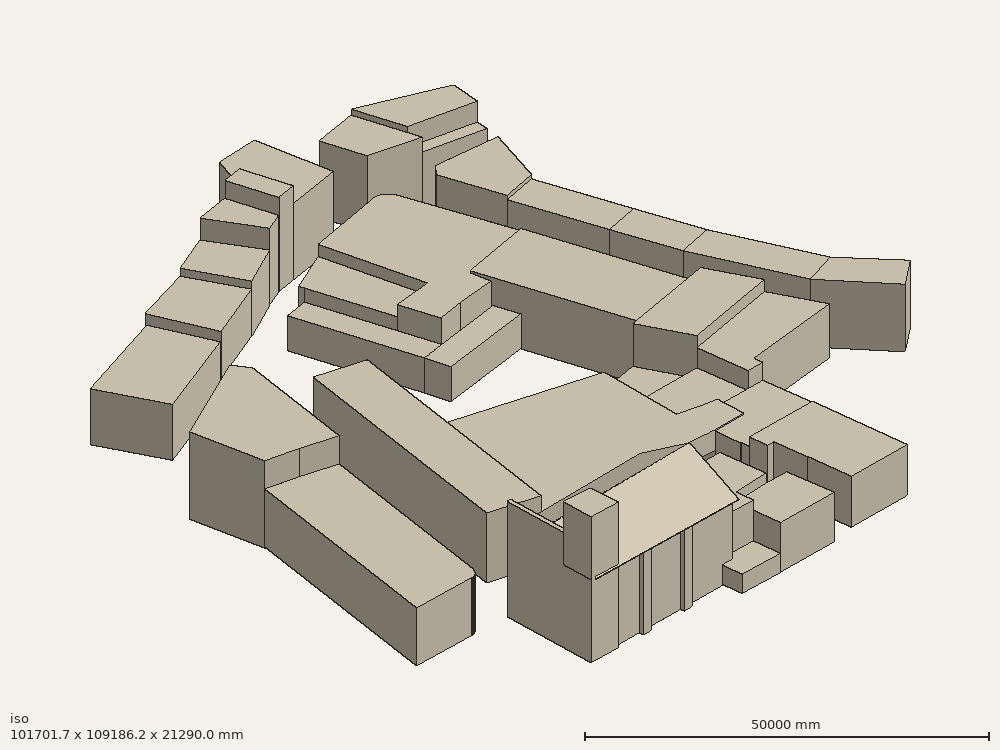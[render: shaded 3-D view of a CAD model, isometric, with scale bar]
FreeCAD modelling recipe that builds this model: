
FCSTD DOCUMENT  (FreeCAD 0.16R6563 (Git))
Label: Levantamento
License: All rights reserved
LicenseURL: http://en.wikipedia.org/wiki/All_rights_reserved
objects: App::Annotation×611, Part::Feature×158, Part::Part2DObjectPython×64, Part::Extrusion×37, App::DocumentObjectGroup×7, Part::FeaturePython×7, App::FeaturePython×4, Part::Cut×2, Part::Compound×1, Part::MultiFuse×1, App::DocumentObjectGroupPython×1
note: 273 computed .brp shape members not serialized (recipe doc carries the construction recipe); baked Part::Feature solids carry a one-line shape summary decoded from their .brp

FEATURE [App::Annotation] Text
  LabelText = TRAVESSA DE S.TIAGO
  Position = (-9.7511e+07,-6.33971e+07,25950)
FEATURE [App::Annotation] Text001
  LabelText = LARGO DR. JUSTINO FREIRE
  Position = (-9.75583e+07,-6.3388e+07,26154)
FEATURE [App::Annotation] Text002
  LabelText = RUA DO ALEIXO
  Position = (-9.75352e+07,-6.33613e+07,25958)
FEATURE [App::Annotation] Text003
  LabelText = RUA DO TERREIRINHO
  Position = (-9.75126e+07,-6.33096e+07,25667)
FEATURE [App::Annotation] Text004
  LabelText = RUA SERPA PINTO
  Position = (-9.74773e+07,-6.3325e+07,26806)
FEATURE [App::Annotation] Text005
  LabelText = IGREJA DE S. TIAGO
  Position = (-9.75165e+07,-6.33832e+07,25950)
FEATURE [App::Annotation] Text006
  LabelText = -97400
  Position = (-9.74009e+07,-6.34097e+07,0)
FEATURE [App::Annotation] Text007
  LabelText = -97450
  Position = (-9.74508e+07,-6.34097e+07,0)
FEATURE [App::Annotation] Text008
  LabelText = -97500
  Position = (-9.75009e+07,-6.34097e+07,0)
FEATURE [App::Annotation] Text009
  LabelText = -97550
  Position = (-9.75507e+07,-6.34097e+07,0)
FEATURE [App::Annotation] Text010
  LabelText = -63400
  Position = (-9.73992e+07,-6.33989e+07,0)
FEATURE [App::Annotation] Text011
  LabelText = -63350
  Position = (-9.73992e+07,-6.33486e+07,0)
FEATURE [App::Annotation] Text012
  LabelText = -63300
  Position = (-9.73992e+07,-6.32985e+07,0)
FEATURE [App::Annotation] Text013
  LabelText = VD
  Position = (-9.75235e+07,-6.33229e+07,0)
FEATURE [App::Annotation] Text014
  LabelText = 25.74
  Position = (-9.75242e+07,-6.33231e+07,0)
FEATURE [App::Annotation] Text015
  LabelText = IN
  Position = (-9.75237e+07,-6.33233e+07,0)
FEATURE [App::Annotation] Text016
  LabelText = 25.75
  Position = (-9.75244e+07,-6.33234e+07,0)
FEATURE [App::Annotation] Text017
  LabelText = LNMRVD
  Position = (-9.75268e+07,-6.3332e+07,0)
FEATURE [App::Annotation] Text018
  LabelText = 25.79
  Position = (-9.75274e+07,-6.33329e+07,0)
FEATURE [App::Annotation] Text019
  LabelText = LN
  Position = (-9.7528e+07,-6.33353e+07,0)
FEATURE [App::Annotation] Text020
  LabelText = 25.72
  Position = (-9.75287e+07,-6.33356e+07,0)
FEATURE [App::Annotation] Text021
  LabelText = 26.02
  Position = (-9.7542e+07,-6.33754e+07,0)
FEATURE [App::Annotation] Text022
  LabelText = CX
  Position = (-9.75309e+07,-6.33164e+07,0)
FEATURE [App::Annotation] Text023
  LabelText = 25.70
  Position = (-9.75313e+07,-6.33168e+07,0)
FEATURE [App::Annotation] Text024
  LabelText = CX
  Position = (-9.75307e+07,-6.33169e+07,0)
FEATURE [App::Annotation] Text025
  LabelText = 25.63
  Position = (-9.75311e+07,-6.33173e+07,0)
FEATURE [App::Annotation] Text026
  LabelText = CX
  Position = (-9.75311e+07,-6.3317e+07,0)
FEATURE [App::Annotation] Text027
  LabelText = 25.63
  Position = (-9.75315e+07,-6.33174e+07,0)
FEATURE [App::Annotation] Text028
  LabelText = CC
  Position = (-9.7534e+07,-6.33179e+07,0)
FEATURE [App::Annotation] Text029
  LabelText = 25.76
  Position = (-9.75346e+07,-6.33182e+07,0)
FEATURE [App::Annotation] Text030
  LabelText = OL
  Position = (-9.75349e+07,-6.33183e+07,0)
FEATURE [App::Annotation] Text031
  LabelText = 26.00
  Position = (-9.75356e+07,-6.33185e+07,0)
FEATURE [App::Annotation] Text032
  LabelText = OL
  Position = (-9.75364e+07,-6.3319e+07,0)
FEATURE [App::Annotation] Text033
  LabelText = 26.00
  Position = (-9.75371e+07,-6.33193e+07,0)
FEATURE [App::Annotation] Text034
  LabelText = LNCC
  Position = (-9.7539e+07,-6.33199e+07,0)
FEATURE [App::Annotation] Text035
  LabelText = 25.84
  Position = (-9.75396e+07,-6.33204e+07,0)
FEATURE [App::Annotation] Text036
  LabelText = LN
  Position = (-9.75385e+07,-6.33211e+07,0)
FEATURE [App::Annotation] Text037
  LabelText = 25.73
  Position = (-9.75392e+07,-6.33213e+07,0)
FEATURE [App::Annotation] Text038
  LabelText = CTT
  Position = (-9.75428e+07,-6.33239e+07,0)
FEATURE [App::Annotation] Text039
  LabelText = 25.88
  Position = (-9.75435e+07,-6.33242e+07,0)
FEATURE [App::Annotation] Text040
  LabelText = CTT
  Position = (-9.75436e+07,-6.33243e+07,0)
FEATURE [App::Annotation] Text041
  LabelText = 25.88
  Position = (-9.75442e+07,-6.33246e+07,0)
FEATURE [App::Annotation] Text042
  LabelText = CTT
  Position = (-9.75439e+07,-6.33237e+07,0)
FEATURE [App::Annotation] Text043
  LabelText = 25.87
  Position = (-9.75445e+07,-6.3324e+07,0)
FEATURE [App::Annotation] Text044
  LabelText = SOL
  Position = (-9.75449e+07,-6.33228e+07,0)
FEATURE [App::Annotation] Text045
  LabelText = 26.13
  Position = (-9.75455e+07,-6.33231e+07,0)
FEATURE [App::Annotation] Text046
  LabelText = LN
  Position = (-9.75498e+07,-6.33263e+07,0)
FEATURE [App::Annotation] Text047
  LabelText = 25.92
  Position = (-9.75505e+07,-6.33265e+07,0)
FEATURE [App::Annotation] Text048
  LabelText = CC
  Position = (-9.75503e+07,-6.33253e+07,0)
FEATURE [App::Annotation] Text049
  LabelText = 26.11
  Position = (-9.75509e+07,-6.33256e+07,0)
FEATURE [App::Annotation] Text050
  LabelText = OL
  Position = (-9.75518e+07,-6.3326e+07,0)
FEATURE [App::Annotation] Text051
  LabelText = 26.19
  Position = (-9.75524e+07,-6.33263e+07,0)
FEATURE [App::Annotation] Text052
  LabelText = CC
  Position = (-9.75559e+07,-6.33278e+07,0)
FEATURE [App::Annotation] Text053
  LabelText = 26.12
  Position = (-9.75565e+07,-6.3328e+07,0)
FEATURE [App::Annotation] Text054
  LabelText = LN
  Position = (-9.75554e+07,-6.33287e+07,0)
FEATURE [App::Annotation] Text055
  LabelText = 25.90
  Position = (-9.75561e+07,-6.33289e+07,0)
FEATURE [App::Annotation] Text056
  LabelText = INH
  Position = (-9.75539e+07,-6.3334e+07,0)
FEATURE [App::Annotation] Text057
  LabelText = 25.92
  Position = (-9.75546e+07,-6.33343e+07,0)
FEATURE [App::Annotation] Text058
  LabelText = INH
  Position = (-9.75549e+07,-6.33321e+07,0)
FEATURE [App::Annotation] Text059
  LabelText = 26.04
  Position = (-9.75555e+07,-6.33324e+07,0)
FEATURE [App::Annotation] Text060
  LabelText = INH
  Position = (-9.75501e+07,-6.33302e+07,0)
FEATURE [App::Annotation] Text061
  LabelText = 26.05
  Position = (-9.75508e+07,-6.33305e+07,0)
FEATURE [App::Annotation] Text062
  LabelText = INH
  Position = (-9.75369e+07,-6.33231e+07,0)
FEATURE [App::Annotation] Text063
  LabelText = 25.84
  Position = (-9.75376e+07,-6.33234e+07,0)
FEATURE [App::Annotation] Text064
  LabelText = INH
  Position = (-9.75357e+07,-6.33232e+07,0)
FEATURE [App::Annotation] Text065
  LabelText = 25.82
  Position = (-9.75363e+07,-6.33235e+07,0)
FEATURE [App::Annotation] Text066
  LabelText = INH
  Position = (-9.75336e+07,-6.33221e+07,0)
FEATURE [App::Annotation] Text067
  LabelText = 25.76
  Position = (-9.75343e+07,-6.33224e+07,0)
FEATURE [App::Annotation] Text068
  LabelText = OL
  Position = (-9.7533e+07,-6.33256e+07,0)
FEATURE [App::Annotation] Text069
  LabelText = 26.42
  Position = (-9.75337e+07,-6.33259e+07,0)
FEATURE [App::Annotation] Text070
  LabelText = IN
  Position = (-9.75314e+07,-6.33278e+07,0)
FEATURE [App::Annotation] Text071
  LabelText = 25.89
  Position = (-9.7532e+07,-6.33279e+07,0)
FEATURE [App::Annotation] Text072
  LabelText = CC
  Position = (-9.75315e+07,-6.33268e+07,0)
FEATURE [App::Annotation] Text073
  LabelText = 25.89
  Position = (-9.75322e+07,-6.33271e+07,0)
FEATURE [App::Annotation] Text074
  LabelText = CC
  Position = (-9.75329e+07,-6.33242e+07,0)
FEATURE [App::Annotation] Text075
  LabelText = 25.84
  Position = (-9.75336e+07,-6.33245e+07,0)
FEATURE [App::Annotation] Text076
  LabelText = CC
  Position = (-9.75382e+07,-6.33271e+07,0)
FEATURE [App::Annotation] Text077
  LabelText = 25.93
  Position = (-9.75388e+07,-6.33273e+07,0)
FEATURE [App::Annotation] Text078
  LabelText = UM
  Position = (-9.75385e+07,-6.33265e+07,0)
FEATURE [App::Annotation] Text079
  LabelText = 25.76
  Position = (-9.75392e+07,-6.33268e+07,0)
FEATURE [App::Annotation] Text080
  LabelText = UM
  Position = (-9.75319e+07,-6.33228e+07,0)
FEATURE [App::Annotation] Text081
  LabelText = 25.67
  Position = (-9.75326e+07,-6.33231e+07,0)
FEATURE [App::Annotation] Text082
  LabelText = UM
  Position = (-9.75313e+07,-6.33232e+07,0)
FEATURE [App::Annotation] Text083
  LabelText = 25.67
  Position = (-9.7532e+07,-6.33235e+07,0)
FEATURE [App::Annotation] Text084
  LabelText = LN
  Position = (-9.75323e+07,-6.33233e+07,0)
FEATURE [App::Annotation] Text085
  LabelText = 25.68
  Position = (-9.7533e+07,-6.33235e+07,0)
FEATURE [App::Annotation] Text086
  LabelText = LN
  Position = (-9.75315e+07,-6.33235e+07,0)
FEATURE [App::Annotation] Text087
  LabelText = 25.72
  Position = (-9.75322e+07,-6.33238e+07,0)
FEATURE [App::Annotation] Text088
  LabelText = LN
  Position = (-9.75305e+07,-6.33251e+07,0)
FEATURE [App::Annotation] Text089
  LabelText = 25.75
  Position = (-9.75311e+07,-6.33253e+07,0)
FEATURE [App::Annotation] Text090
  LabelText = LN
  Position = (-9.75301e+07,-6.33276e+07,0)
FEATURE [App::Annotation] Text091
  LabelText = 25.72
  Position = (-9.75307e+07,-6.33279e+07,0)
FEATURE [App::Annotation] Text092
  LabelText = VD
  Position = (-9.75244e+07,-6.33212e+07,0)
FEATURE [App::Annotation] Text093
  LabelText = 25.72
  Position = (-9.75251e+07,-6.33214e+07,0)
FEATURE [App::Annotation] Text094
  LabelText = CXD
  Position = (-9.75204e+07,-6.33159e+07,0)
FEATURE [App::Annotation] Text095
  LabelText = 25.67
  Position = (-9.75207e+07,-6.33163e+07,0)
FEATURE [App::Annotation] Text096
  LabelText = VD
  Position = (-9.75183e+07,-6.33166e+07,0)
FEATURE [App::Annotation] Text097
  LabelText = 25.58
  Position = (-9.7519e+07,-6.33169e+07,0)
FEATURE [App::Annotation] Text098
  LabelText = OL
  Position = (-9.75059e+07,-6.33029e+07,0)
FEATURE [App::Annotation] Text099
  LabelText = 25.84
  Position = (-9.75065e+07,-6.33031e+07,0)
FEATURE [App::Annotation] Text100
  LabelText = OL
  Position = (-9.75043e+07,-6.33022e+07,0)
FEATURE [App::Annotation] Text101
  LabelText = 25.94
  Position = (-9.75049e+07,-6.33025e+07,0)
FEATURE [App::Annotation] Text102
  LabelText = CXE
  Position = (-9.7504e+07,-6.33017e+07,0)
FEATURE [App::Annotation] Text103
  LabelText = 25.84
  Position = (-9.75043e+07,-6.33021e+07,0)
FEATURE [App::Annotation] Text104
  LabelText = CXE
  Position = (-9.75038e+07,-6.3302e+07,0)
FEATURE [App::Annotation] Text105
  LabelText = 25.79
  Position = (-9.75041e+07,-6.33024e+07,0)
FEATURE [App::Annotation] Text106
  LabelText = CXE
  Position = (-9.7503e+07,-6.33016e+07,0)
FEATURE [App::Annotation] Text107
  LabelText = 25.80
  Position = (-9.75033e+07,-6.3302e+07,0)
FEATURE [App::Annotation] Text108
  LabelText = OL
  Position = (-9.7499e+07,-6.32997e+07,0)
FEATURE [App::Annotation] Text109
  LabelText = 26.17
  Position = (-9.74996e+07,-6.32999e+07,0)
FEATURE [App::Annotation] Text110
  LabelText = CXD
  Position = (-9.75007e+07,-6.33004e+07,0)
FEATURE [App::Annotation] Text111
  LabelText = 25.85
  Position = (-9.7501e+07,-6.3301e+07,0)
FEATURE [App::Annotation] Text112
  LabelText = CXD
  Position = (-9.74978e+07,-6.32998e+07,0)
FEATURE [App::Annotation] Text113
  LabelText = 25.86
  Position = (-9.74982e+07,-6.33003e+07,0)
FEATURE [App::Annotation] Text114
  LabelText = UM
  Position = (-9.74967e+07,-6.33e+07,0)
FEATURE [App::Annotation] Text115
  LabelText = 25.80
  Position = (-9.74974e+07,-6.33003e+07,0)
FEATURE [App::Annotation] Text116
  LabelText = UM
  Position = (-9.74961e+07,-6.32999e+07,0)
FEATURE [App::Annotation] Text117
  LabelText = 25.79
  Position = (-9.74968e+07,-6.33001e+07,0)
FEATURE [App::Annotation] Text118
  LabelText = IN
  Position = (-9.74906e+07,-6.32984e+07,0)
FEATURE [App::Annotation] Text119
  LabelText = 26.00
  Position = (-9.74913e+07,-6.32985e+07,0)
FEATURE [App::Annotation] Text120
  LabelText = CC
  Position = (-9.74881e+07,-6.32975e+07,0)
FEATURE [App::Annotation] Text121
  LabelText = 26.01
  Position = (-9.74887e+07,-6.32978e+07,0)
FEATURE [App::Annotation] Text122
  LabelText = VD
  Position = (-9.74883e+07,-6.33016e+07,0)
FEATURE [App::Annotation] Text123
  LabelText = 26.02
  Position = (-9.7489e+07,-6.33019e+07,0)
FEATURE [App::Annotation] Text124
  LabelText = VD
  Position = (-9.74956e+07,-6.33036e+07,0)
FEATURE [App::Annotation] Text125
  LabelText = 25.93
  Position = (-9.74963e+07,-6.33039e+07,0)
FEATURE [App::Annotation] Text126
  LabelText = VD
  Position = (-9.74956e+07,-6.33036e+07,0)
FEATURE [App::Annotation] Text127
  LabelText = 25.93
  Position = (-9.74963e+07,-6.33039e+07,0)
FEATURE [App::Annotation] Text128
  LabelText = CXD
  Position = (-9.75007e+07,-6.33052e+07,0)
FEATURE [App::Annotation] Text129
  LabelText = 25.82
  Position = (-9.7501e+07,-6.33056e+07,0)
FEATURE [App::Annotation] Text130
  LabelText = VD
  Position = (-9.75015e+07,-6.33054e+07,0)
FEATURE [App::Annotation] Text131
  LabelText = 25.83
  Position = (-9.75022e+07,-6.33057e+07,0)
FEATURE [App::Annotation] Text132
  LabelText = VD
  Position = (-9.75047e+07,-6.33071e+07,0)
FEATURE [App::Annotation] Text133
  LabelText = 25.76
  Position = (-9.75053e+07,-6.33073e+07,0)
FEATURE [App::Annotation] Text134
  LabelText = CC
  Position = (-9.74996e+07,-6.33064e+07,0)
FEATURE [App::Annotation] Text135
  LabelText = 25.89
  Position = (-9.75003e+07,-6.33067e+07,0)
FEATURE [App::Annotation] Text136
  LabelText = VD
  Position = (-9.75005e+07,-6.33068e+07,0)
FEATURE [App::Annotation] Text137
  LabelText = 25.84
  Position = (-9.75012e+07,-6.3307e+07,0)
FEATURE [App::Annotation] Text138
  LabelText = MRVD
  Position = (-9.75264e+07,-6.33325e+07,0)
FEATURE [App::Annotation] Text139
  LabelText = 26.39
  Position = (-9.7527e+07,-6.33331e+07,0)
FEATURE [App::Annotation] Text140
  LabelText = CT
  Position = (-9.75249e+07,-6.33283e+07,0)
FEATURE [App::Annotation] Text141
  LabelText = 26.35
  Position = (-9.75255e+07,-6.33286e+07,0)
FEATURE [App::Annotation] Text142
  LabelText = CT
  Position = (-9.75222e+07,-6.33238e+07,0)
FEATURE [App::Annotation] Text143
  LabelText = 26.29
  Position = (-9.75229e+07,-6.3324e+07,0)
FEATURE [App::Annotation] Text144
  LabelText = CT
  Position = (-9.75189e+07,-6.33204e+07,0)
FEATURE [App::Annotation] Text145
  LabelText = 26.22
  Position = (-9.75196e+07,-6.33206e+07,0)
FEATURE [App::Annotation] Text146
  LabelText = CT
  Position = (-9.75162e+07,-6.33183e+07,0)
FEATURE [App::Annotation] Text147
  LabelText = 26.20
  Position = (-9.75169e+07,-6.33186e+07,0)
FEATURE [App::Annotation] Text148
  LabelText = CT
  Position = (-9.75164e+07,-6.33162e+07,0)
FEATURE [App::Annotation] Text149
  LabelText = 26.04
  Position = (-9.75171e+07,-6.33165e+07,0)
FEATURE [App::Annotation] Text150
  LabelText = CT
  Position = (-9.75151e+07,-6.33153e+07,0)
FEATURE [App::Annotation] Text151
  LabelText = 26.08
  Position = (-9.75157e+07,-6.33155e+07,0)
FEATURE [App::Annotation] Text152
  LabelText = IL
  Position = (-9.75163e+07,-6.33171e+07,0)
FEATURE [App::Annotation] Text153
  LabelText = 26.13
  Position = (-9.75169e+07,-6.33173e+07,0)
FEATURE [App::Annotation] Text154
  LabelText = IL
  Position = (-9.75157e+07,-6.3316e+07,0)
FEATURE [App::Annotation] Text155
  LabelText = 26.09
  Position = (-9.75164e+07,-6.33161e+07,0)
FEATURE [App::Annotation] Text156
  LabelText = CC
  Position = (-9.75107e+07,-6.33057e+07,0)
FEATURE [App::Annotation] Text157
  LabelText = 25.68
  Position = (-9.75113e+07,-6.3306e+07,0)
FEATURE [App::Annotation] Text158
  LabelText = AT
  Position = (-9.75124e+07,-6.33068e+07,0)
FEATURE [App::Annotation] Text159
  LabelText = 25.58
  Position = (-9.75131e+07,-6.33071e+07,0)
FEATURE [App::Annotation] Text160
  LabelText = OL
  Position = (-9.75161e+07,-6.33083e+07,0)
FEATURE [App::Annotation] Text161
  LabelText = 25.81
  Position = (-9.75167e+07,-6.33085e+07,0)
FEATURE [App::Annotation] Text162
  LabelText = AT
  Position = (-9.75195e+07,-6.33102e+07,0)
FEATURE [App::Annotation] Text163
  LabelText = 25.48
  Position = (-9.75202e+07,-6.33104e+07,0)
FEATURE [App::Annotation] Text164
  LabelText = CXCTT
  Position = (-9.75202e+07,-6.331e+07,0)
FEATURE [App::Annotation] Text165
  LabelText = 25.48
  Position = (-9.75202e+07,-6.33104e+07,0)
FEATURE [App::Annotation] Text166
  LabelText = CXCTT
  Position = (-9.75206e+07,-6.33102e+07,0)
FEATURE [App::Annotation] Text167
  LabelText = 25.47
  Position = (-9.75206e+07,-6.33106e+07,0)
FEATURE [App::Annotation] Text168
  LabelText = UM
  Position = (-9.75203e+07,-6.33103e+07,0)
FEATURE [App::Annotation] Text169
  LabelText = 25.38
  Position = (-9.7521e+07,-6.33106e+07,0)
FEATURE [App::Annotation] Text170
  LabelText = CC
  Position = (-9.75208e+07,-6.33104e+07,0)
FEATURE [App::Annotation] Text171
  LabelText = 25.47
  Position = (-9.75214e+07,-6.33106e+07,0)
FEATURE [App::Annotation] Text172
  LabelText = CTT
  Position = (-9.7521e+07,-6.33111e+07,0)
FEATURE [App::Annotation] Text173
  LabelText = 25.54
  Position = (-9.75216e+07,-6.33115e+07,0)
FEATURE [App::Annotation] Text174
  LabelText = CTT
  Position = (-9.75215e+07,-6.33114e+07,0)
FEATURE [App::Annotation] Text175
  LabelText = 25.57
  Position = (-9.75222e+07,-6.33118e+07,0)
FEATURE [App::Annotation] Text176
  LabelText = CTT
  Position = (-9.7522e+07,-6.33107e+07,0)
FEATURE [App::Annotation] Text177
  LabelText = 25.55
  Position = (-9.75226e+07,-6.3311e+07,0)
FEATURE [App::Annotation] Text178
  LabelText = CC
  Position = (-9.75249e+07,-6.33104e+07,0)
FEATURE [App::Annotation] Text179
  LabelText = 25.65
  Position = (-9.75256e+07,-6.33106e+07,0)
FEATURE [App::Annotation] Text180
  LabelText = OL
  Position = (-9.75244e+07,-6.33121e+07,0)
FEATURE [App::Annotation] Text181
  LabelText = 26.10
  Position = (-9.7525e+07,-6.33123e+07,0)
FEATURE [App::Annotation] Text182
  LabelText = G
  Position = (-9.7524e+07,-6.33116e+07,0)
FEATURE [App::Annotation] Text183
  LabelText = 25.61
  Position = (-9.75246e+07,-6.33117e+07,0)
FEATURE [App::Annotation] Text184
  LabelText = G
  Position = (-9.75238e+07,-6.33122e+07,0)
FEATURE [App::Annotation] Text185
  LabelText = G
  Position = (-9.7524e+07,-6.33123e+07,0)
FEATURE [App::Annotation] Text186
  LabelText = CC
  Position = (-9.75238e+07,-6.33134e+07,0)
FEATURE [App::Annotation] Text187
  LabelText = 25.54
  Position = (-9.75245e+07,-6.33136e+07,0)
FEATURE [App::Annotation] Text188
  LabelText = UM
  Position = (-9.75246e+07,-6.33138e+07,0)
FEATURE [App::Annotation] Text189
  LabelText = 25.52
  Position = (-9.75253e+07,-6.33141e+07,0)
FEATURE [App::Annotation] Text190
  LabelText = SOL
  Position = (-9.75262e+07,-6.33143e+07,0)
FEATURE [App::Annotation] Text191
  LabelText = 25.98
  Position = (-9.75268e+07,-6.33146e+07,0)
FEATURE [App::Annotation] Text192
  LabelText = CXE
  Position = (-9.75276e+07,-6.33148e+07,0)
FEATURE [App::Annotation] Text193
  LabelText = 25.69
  Position = (-9.75279e+07,-6.33152e+07,0)
FEATURE [App::Annotation] Text194
  LabelText = CXE
  Position = (-9.75275e+07,-6.33151e+07,0)
FEATURE [App::Annotation] Text195
  LabelText = 25.63
  Position = (-9.75278e+07,-6.33155e+07,0)
FEATURE [App::Annotation] Text196
  LabelText = CXE
  Position = (-9.75282e+07,-6.33154e+07,0)
FEATURE [App::Annotation] Text197
  LabelText = 25.63
  Position = (-9.75286e+07,-6.33158e+07,0)
FEATURE [App::Annotation] Text198
  LabelText = VD
  Position = (-9.75189e+07,-6.33146e+07,0)
FEATURE [App::Annotation] Text199
  LabelText = 25.64
  Position = (-9.75196e+07,-6.33149e+07,0)
FEATURE [App::Annotation] Text200
  LabelText = VD
  Position = (-9.75178e+07,-6.33139e+07,0)
FEATURE [App::Annotation] Text201
  LabelText = 25.69
  Position = (-9.75185e+07,-6.33141e+07,0)
FEATURE [App::Annotation] Text202
  LabelText = VD
  Position = (-9.75147e+07,-6.33122e+07,0)
FEATURE [App::Annotation] Text203
  LabelText = 25.65
  Position = (-9.75154e+07,-6.33124e+07,0)
FEATURE [App::Annotation] Text204
  LabelText = 25.59
  Position = (-9.75159e+07,-6.3314e+07,0)
FEATURE [App::Annotation] Text205
  LabelText = VD
  Position = (-9.75151e+07,-6.33139e+07,0)
FEATURE [App::Annotation] Text206
  LabelText = 25.60
  Position = (-9.75158e+07,-6.33142e+07,0)
FEATURE [App::Annotation] Text207
  LabelText = G
  Position = (-9.75151e+07,-6.33144e+07,0)
FEATURE [App::Annotation] Text208
  LabelText = 25.62
  Position = (-9.75158e+07,-6.33145e+07,0)
FEATURE [App::Annotation] Text209
  LabelText = G
  Position = (-9.7515e+07,-6.33146e+07,0)
FEATURE [App::Annotation] Text210
  LabelText = 25.81
  Position = (-9.75156e+07,-6.33147e+07,0)
FEATURE [App::Annotation] Text211
  LabelText = G
  Position = (-9.75148e+07,-6.3315e+07,0)
FEATURE [App::Annotation] Text212
  LabelText = 26.13
  Position = (-9.75154e+07,-6.33151e+07,0)
FEATURE [App::Annotation] Text213
  LabelText = G
  Position = (-9.75121e+07,-6.33136e+07,0)
FEATURE [App::Annotation] Text214
  LabelText = 26.12
  Position = (-9.75128e+07,-6.33137e+07,0)
FEATURE [App::Annotation] Text215
  LabelText = G
  Position = (-9.75123e+07,-6.33134e+07,0)
FEATURE [App::Annotation] Text216
  LabelText = 25.82
  Position = (-9.7513e+07,-6.33135e+07,0)
FEATURE [App::Annotation] Text217
  LabelText = G
  Position = (-9.75124e+07,-6.33131e+07,0)
FEATURE [App::Annotation] Text218
  LabelText = 25.65
  Position = (-9.75131e+07,-6.33132e+07,0)
FEATURE [App::Annotation] Text219
  LabelText = AMP
  Position = (-9.75137e+07,-6.33114e+07,0)
FEATURE [App::Annotation] Text220
  LabelText = 25.69
  Position = (-9.75144e+07,-6.33119e+07,0)
FEATURE [App::Annotation] Text221
  LabelText = AMP
  Position = (-9.75064e+07,-6.33077e+07,0)
FEATURE [App::Annotation] Text222
  LabelText = 25.77
  Position = (-9.75071e+07,-6.33081e+07,0)
FEATURE [App::Annotation] Text223
  LabelText = VD
  Position = (-9.7506e+07,-6.33096e+07,0)
FEATURE [App::Annotation] Text224
  LabelText = 25.99
  Position = (-9.75067e+07,-6.33099e+07,0)
FEATURE [App::Annotation] Text225
  LabelText = MR
  Position = (-9.7506e+07,-6.33102e+07,0)
FEATURE [App::Annotation] Text226
  LabelText = 26.07
  Position = (-9.75067e+07,-6.33104e+07,0)
FEATURE [App::Annotation] Text227
  LabelText = MRCC
  Position = (-9.75003e+07,-6.33069e+07,0)
FEATURE [App::Annotation] Text228
  LabelText = 26.23
  Position = (-9.7501e+07,-6.33075e+07,0)
FEATURE [App::Annotation] Text229
  LabelText = ESTMR
  Position = (-9.75051e+07,-6.33093e+07,0)
FEATURE [App::Annotation] Text230
  LabelText = 26.13
  Position = (-9.75051e+07,-6.33097e+07,0)
FEATURE [App::Annotation] Text231
  LabelText = EST
  Position = (-9.7502e+07,-6.33232e+07,0)
FEATURE [App::Annotation] Text232
  LabelText = 26.32
  Position = (-9.75023e+07,-6.33236e+07,0)
FEATURE [App::Annotation] Text233
  LabelText = CC
  Position = (-9.74969e+07,-6.33227e+07,0)
FEATURE [App::Annotation] Text234
  LabelText = 26.61
  Position = (-9.74975e+07,-6.3323e+07,0)
FEATURE [App::Annotation] Text235
  LabelText = IN20
  Position = (-9.74775e+07,-6.33355e+07,0)
FEATURE [App::Annotation] Text236
  LabelText = 26.83
  Position = (-9.74781e+07,-6.3336e+07,0)
FEATURE [App::Annotation] Text237
  LabelText = IN20
  Position = (-9.74755e+07,-6.33426e+07,0)
FEATURE [App::Annotation] Text238
  LabelText = 26.90
  Position = (-9.74762e+07,-6.3343e+07,0)
FEATURE [App::Annotation] Text239
  LabelText = IN20
  Position = (-9.74749e+07,-6.3345e+07,0)
FEATURE [App::Annotation] Text240
  LabelText = 26.90
  Position = (-9.74755e+07,-6.33455e+07,0)
FEATURE [App::Annotation] Text241
  LabelText = OL
  Position = (-9.7472e+07,-6.33367e+07,0)
FEATURE [App::Annotation] Text242
  LabelText = 26.86
  Position = (-9.74727e+07,-6.33369e+07,0)
FEATURE [App::Annotation] Text243
  LabelText = ESG
  Position = (-9.7474e+07,-6.33311e+07,0)
FEATURE [App::Annotation] Text244
  LabelText = 26.39
  Position = (-9.74743e+07,-6.33315e+07,0)
FEATURE [App::Annotation] Text245
  LabelText = OL
  Position = (-9.74741e+07,-6.3329e+07,0)
FEATURE [App::Annotation] Text246
  LabelText = 26.56
  Position = (-9.74748e+07,-6.33293e+07,0)
FEATURE [App::Annotation] Text247
  LabelText = OL
  Position = (-9.74748e+07,-6.33265e+07,0)
FEATURE [App::Annotation] Text248
  LabelText = 26.58
  Position = (-9.74754e+07,-6.33267e+07,0)
FEATURE [App::Annotation] Text249
  LabelText = OL
  Position = (-9.74762e+07,-6.33213e+07,0)
FEATURE [App::Annotation] Text250
  LabelText = 26.54
  Position = (-9.74768e+07,-6.33215e+07,0)
FEATURE [App::Annotation] Text251
  LabelText = CC
  Position = (-9.74793e+07,-6.33223e+07,0)
FEATURE [App::Annotation] Text252
  LabelText = 26.39
  Position = (-9.748e+07,-6.33225e+07,0)
FEATURE [App::Annotation] Text253
  LabelText = AT
  Position = (-9.74791e+07,-6.33222e+07,0)
FEATURE [App::Annotation] Text254
  LabelText = 26.35
  Position = (-9.74798e+07,-6.33225e+07,0)
FEATURE [App::Annotation] Text255
  LabelText = AT
  Position = (-9.74772e+07,-6.33305e+07,0)
FEATURE [App::Annotation] Text256
  LabelText = 26.52
  Position = (-9.74779e+07,-6.33307e+07,0)
FEATURE [App::Annotation] Text257
  LabelText = UM25
  Position = (-9.74767e+07,-6.33302e+07,0)
FEATURE [App::Annotation] Text258
  LabelText = 26.44
  Position = (-9.74774e+07,-6.33308e+07,0)
FEATURE [App::Annotation] Text259
  LabelText = UM25
  Position = (-9.74765e+07,-6.33309e+07,0)
FEATURE [App::Annotation] Text260
  LabelText = 26.47
  Position = (-9.74772e+07,-6.33315e+07,0)
FEATURE [App::Annotation] Text261
  LabelText = UM25
  Position = (-9.74765e+07,-6.33309e+07,0)
FEATURE [App::Annotation] Text262
  LabelText = 26.47
  Position = (-9.74772e+07,-6.33315e+07,0)
FEATURE [App::Annotation] Text263
  LabelText = CC
  Position = (-9.74772e+07,-6.33312e+07,0)
FEATURE [App::Annotation] Text264
  LabelText = 26.51
  Position = (-9.74778e+07,-6.33314e+07,0)
FEATURE [App::Annotation] Text265
  LabelText = AT
  Position = (-9.74769e+07,-6.33311e+07,0)
FEATURE [App::Annotation] Text266
  LabelText = 26.50
  Position = (-9.74776e+07,-6.33314e+07,0)
FEATURE [App::Annotation] Text267
  LabelText = AT
  Position = (-9.74755e+07,-6.33378e+07,0)
FEATURE [App::Annotation] Text268
  LabelText = 26.62
  Position = (-9.74761e+07,-6.33381e+07,0)
FEATURE [App::Annotation] Text269
  LabelText = AT
  Position = (-9.74751e+07,-6.33389e+07,0)
FEATURE [App::Annotation] Text270
  LabelText = 26.69
  Position = (-9.74758e+07,-6.33391e+07,0)
FEATURE [App::Annotation] Text271
  LabelText = CX
  Position = (-9.74751e+07,-6.33372e+07,0)
FEATURE [App::Annotation] Text272
  LabelText = 26.61
  Position = (-9.74754e+07,-6.33376e+07,0)
FEATURE [App::Annotation] Text273
  LabelText = OL
  Position = (-9.74711e+07,-6.33401e+07,0)
FEATURE [App::Annotation] Text274
  LabelText = 26.84
  Position = (-9.74718e+07,-6.33404e+07,0)
FEATURE [App::Annotation] Text275
  LabelText = UM25
  Position = (-9.74713e+07,-6.33411e+07,0)
FEATURE [App::Annotation] Text276
  LabelText = 26.71
  Position = (-9.74719e+07,-6.33416e+07,0)
FEATURE [App::Annotation] Text277
  LabelText = UM25
  Position = (-9.74711e+07,-6.33417e+07,0)
FEATURE [App::Annotation] Text278
  LabelText = 26.73
  Position = (-9.74718e+07,-6.33423e+07,0)
FEATURE [App::Annotation] Text279
  LabelText = CC
  Position = (-9.74707e+07,-6.3342e+07,0)
FEATURE [App::Annotation] Text280
  LabelText = 26.76
  Position = (-9.74714e+07,-6.33422e+07,0)
FEATURE [App::Annotation] Text281
  LabelText = OL
  Position = (-9.74678e+07,-6.33494e+07,0)
FEATURE [App::Annotation] Text282
  LabelText = 27.04
  Position = (-9.74685e+07,-6.33497e+07,0)
FEATURE [App::Annotation] Text283
  LabelText = CX
  Position = (-9.74687e+07,-6.33501e+07,0)
FEATURE [App::Annotation] Text284
  LabelText = 27.04
  Position = (-9.74691e+07,-6.33505e+07,0)
FEATURE [App::Annotation] Text285
  LabelText = CC
  Position = (-9.74661e+07,-6.33623e+07,0)
FEATURE [App::Annotation] Text286
  LabelText = 27.55
  Position = (-9.74668e+07,-6.33626e+07,0)
FEATURE [App::Annotation] Text287
  LabelText = OL
  Position = (-9.74678e+07,-6.33585e+07,0)
FEATURE [App::Annotation] Text288
  LabelText = 27.40
  Position = (-9.74685e+07,-6.33587e+07,0)
FEATURE [App::Annotation] Text289
  LabelText = OL
  Position = (-9.74727e+07,-6.33483e+07,0)
FEATURE [App::Annotation] Text290
  LabelText = 27.14
  Position = (-9.74734e+07,-6.33485e+07,0)
FEATURE [App::Annotation] Text291
  LabelText = CX
  Position = (-9.74726e+07,-6.33461e+07,0)
FEATURE [App::Annotation] Text292
  LabelText = 26.85
  Position = (-9.7473e+07,-6.33465e+07,0)
FEATURE [App::Annotation] Text293
  LabelText = UM25
  Position = (-9.74731e+07,-6.3345e+07,0)
FEATURE [App::Annotation] Text294
  LabelText = 26.81
  Position = (-9.74736e+07,-6.33456e+07,0)
FEATURE [App::Annotation] Text295
  LabelText = UM25
  Position = (-9.74729e+07,-6.33456e+07,0)
FEATURE [App::Annotation] Text296
  LabelText = 26.80
  Position = (-9.74736e+07,-6.33462e+07,0)
FEATURE [App::Annotation] Text297
  LabelText = AT
  Position = (-9.74731e+07,-6.33466e+07,0)
FEATURE [App::Annotation] Text298
  LabelText = 26.87
  Position = (-9.74737e+07,-6.33469e+07,0)
FEATURE [App::Annotation] Text299
  LabelText = CC
  Position = (-9.74731e+07,-6.3347e+07,0)
FEATURE [App::Annotation] Text300
  LabelText = 26.89
  Position = (-9.74738e+07,-6.33472e+07,0)
FEATURE [App::Annotation] Text301
  LabelText = CC
  Position = (-9.74733e+07,-6.33461e+07,0)
FEATURE [App::Annotation] Text302
  LabelText = 26.87
  Position = (-9.7474e+07,-6.33463e+07,0)
FEATURE [App::Annotation] Text303
  LabelText = CC30
  Position = (-9.74747e+07,-6.33462e+07,0)
FEATURE [App::Annotation] Text304
  LabelText = 26.91
  Position = (-9.74752e+07,-6.33467e+07,0)
FEATURE [App::Annotation] Text305
  LabelText = EST
  Position = (-9.75057e+07,-6.33385e+07,0)
FEATURE [App::Annotation] Text306
  LabelText = CC
  Position = (-9.75033e+07,-6.33238e+07,0)
FEATURE [App::Annotation] Text307
  LabelText = 26.29
  Position = (-9.75039e+07,-6.33241e+07,0)
FEATURE [App::Annotation] Text308
  LabelText = ESTA
  Position = (-9.75136e+07,-6.33216e+07,0)
FEATURE [App::Annotation] Text309
  LabelText = 26.22
  Position = (-9.75138e+07,-6.3322e+07,0)
FEATURE [App::Annotation] Text310
  LabelText = ESTA
  Position = (-9.75146e+07,-6.33204e+07,0)
FEATURE [App::Annotation] Text311
  LabelText = 26.22
  Position = (-9.75147e+07,-6.33208e+07,0)
FEATURE [App::Annotation] Text312
  LabelText = ESTA
  Position = (-9.75106e+07,-6.33181e+07,0)
FEATURE [App::Annotation] Text313
  LabelText = 26.19
  Position = (-9.75107e+07,-6.33185e+07,0)
FEATURE [App::Annotation] Text314
  LabelText = ESTA
  Position = (-9.75125e+07,-6.33137e+07,0)
FEATURE [App::Annotation] Text315
  LabelText = 26.09
  Position = (-9.75127e+07,-6.33141e+07,0)
FEATURE [App::Annotation] Text316
  LabelText = ESTA
  Position = (-9.75168e+07,-6.33177e+07,0)
FEATURE [App::Annotation] Text317
  LabelText = 26.15
  Position = (-9.75169e+07,-6.33181e+07,0)
FEATURE [App::Annotation] Text318
  LabelText = ESTA
  Position = (-9.75135e+07,-6.33216e+07,0)
FEATURE [App::Annotation] Text319
  LabelText = 26.22
  Position = (-9.75137e+07,-6.3322e+07,0)
FEATURE [App::Annotation] Text320
  LabelText = ESTA
  Position = (-9.75199e+07,-6.33285e+07,0)
FEATURE [App::Annotation] Text321
  LabelText = 26.34
  Position = (-9.75201e+07,-6.33289e+07,0)
FEATURE [App::Annotation] Text322
  LabelText = ESTA
  Position = (-9.75246e+07,-6.33266e+07,0)
FEATURE [App::Annotation] Text323
  LabelText = 26.29
  Position = (-9.75248e+07,-6.3327e+07,0)
FEATURE [App::Annotation] Text324
  LabelText = ESTA
  Position = (-9.75272e+07,-6.33333e+07,0)
FEATURE [App::Annotation] Text325
  LabelText = 26.37
  Position = (-9.75274e+07,-6.33337e+07,0)
FEATURE [App::Annotation] Text326
  LabelText = ESTA
  Position = (-9.75217e+07,-6.33327e+07,0)
FEATURE [App::Annotation] Text327
  LabelText = 26.38
  Position = (-9.75219e+07,-6.33331e+07,0)
FEATURE [App::Annotation] Text328
  LabelText = ESTA
  Position = (-9.75307e+07,-6.33502e+07,0)
FEATURE [App::Annotation] Text329
  LabelText = 26.37
  Position = (-9.75309e+07,-6.33506e+07,0)
FEATURE [App::Annotation] Text330
  LabelText = ESTA
  Position = (-9.75255e+07,-6.33497e+07,0)
FEATURE [App::Annotation] Text331
  LabelText = 26.34
  Position = (-9.75257e+07,-6.33501e+07,0)
FEATURE [App::Annotation] Text332
  LabelText = ESTA1
  Position = (-9.75292e+07,-6.33666e+07,0)
FEATURE [App::Annotation] Text333
  LabelText = 26.09
  Position = (-9.75293e+07,-6.3367e+07,0)
FEATURE [App::Annotation] Text334
  LabelText = ESTA1
  Position = (-9.75342e+07,-6.33669e+07,0)
FEATURE [App::Annotation] Text335
  LabelText = 26.08
  Position = (-9.75343e+07,-6.33673e+07,0)
FEATURE [App::Annotation] Text336
  LabelText = ESTA1
  Position = (-9.75059e+07,-6.33539e+07,0)
FEATURE [App::Annotation] Text337
  LabelText = 26.29
  Position = (-9.7506e+07,-6.33543e+07,0)
FEATURE [App::Annotation] Text338
  LabelText = ESTA1
  Position = (-9.75009e+07,-6.33537e+07,0)
FEATURE [App::Annotation] Text339
  LabelText = 26.37
  Position = (-9.7501e+07,-6.33541e+07,0)
FEATURE [App::Annotation] Text340
  LabelText = ESTA1
  Position = (-9.75013e+07,-6.33551e+07,0)
FEATURE [App::Annotation] Text341
  LabelText = 26.35
  Position = (-9.75014e+07,-6.33555e+07,0)
FEATURE [App::Annotation] Text342
  LabelText = ESTA1
  Position = (-9.7499e+07,-6.33554e+07,0)
FEATURE [App::Annotation] Text343
  LabelText = 26.41
  Position = (-9.74991e+07,-6.33558e+07,0)
FEATURE [App::Annotation] Text344
  LabelText = ESTA1
  Position = (-9.75019e+07,-6.33694e+07,0)
FEATURE [App::Annotation] Text345
  LabelText = 26.33
  Position = (-9.7502e+07,-6.33698e+07,0)
FEATURE [App::Annotation] Text346
  LabelText = ESTA1
  Position = (-9.75042e+07,-6.33689e+07,0)
FEATURE [App::Annotation] Text347
  LabelText = 26.31
  Position = (-9.75042e+07,-6.33693e+07,0)
FEATURE [App::Annotation] Text348
  LabelText = ESTA1
  Position = (-9.75046e+07,-6.33704e+07,0)
FEATURE [App::Annotation] Text349
  LabelText = 26.31
  Position = (-9.75046e+07,-6.33708e+07,0)
FEATURE [App::Annotation] Text350
  LabelText = ESTA1
  Position = (-9.75096e+07,-6.33706e+07,0)
FEATURE [App::Annotation] Text351
  LabelText = 26.24
  Position = (-9.75097e+07,-6.33715e+07,0)
FEATURE [App::Annotation] Text352
  LabelText = ESTA
  Position = (-9.7515e+07,-6.33713e+07,0)
FEATURE [App::Annotation] Text353
  LabelText = 26.19
  Position = (-9.75151e+07,-6.33722e+07,0)
FEATURE [App::Annotation] Text354
  LabelText = ESTA
  Position = (-9.75098e+07,-6.33473e+07,0)
FEATURE [App::Annotation] Text355
  LabelText = 26.37
  Position = (-9.751e+07,-6.33477e+07,0)
FEATURE [App::Annotation] Text356
  LabelText = ESTA
  Position = (-9.7514e+07,-6.33445e+07,0)
FEATURE [App::Annotation] Text357
  LabelText = 26.40
  Position = (-9.75142e+07,-6.33449e+07,0)
FEATURE [App::Annotation] Text358
  LabelText = ESTA
  Position = (-9.75182e+07,-6.33417e+07,0)
FEATURE [App::Annotation] Text359
  LabelText = 26.39
  Position = (-9.75184e+07,-6.33421e+07,0)
FEATURE [App::Annotation] Text360
  LabelText = ESTA
  Position = (-9.75156e+07,-6.33297e+07,0)
FEATURE [App::Annotation] Text361
  LabelText = 26.37
  Position = (-9.75158e+07,-6.33301e+07,0)
FEATURE [App::Annotation] Text362
  LabelText = ESTA
  Position = (-9.75134e+07,-6.33311e+07,0)
FEATURE [App::Annotation] Text363
  LabelText = 26.37
  Position = (-9.75136e+07,-6.33315e+07,0)
FEATURE [App::Annotation] Text364
  LabelText = ESTA
  Position = (-9.75125e+07,-6.33262e+07,0)
FEATURE [App::Annotation] Text365
  LabelText = 26.30
  Position = (-9.75127e+07,-6.33266e+07,0)
FEATURE [App::Annotation] Text366
  LabelText = ESTA
  Position = (-9.75061e+07,-6.33303e+07,0)
FEATURE [App::Annotation] Text367
  LabelText = 26.34
  Position = (-9.75063e+07,-6.33307e+07,0)
FEATURE [App::Annotation] Text368
  LabelText = EST
  Position = (-9.75055e+07,-6.3311e+07,0)
FEATURE [App::Annotation] Text369
  LabelText = 26.14
  Position = (-9.75065e+07,-6.33115e+07,0)
FEATURE [App::Annotation] Text370
  LabelText = ESTA
  Position = (-9.75e+07,-6.3334e+07,0)
FEATURE [App::Annotation] Text371
  LabelText = 26.46
  Position = (-9.75001e+07,-6.33344e+07,0)
FEATURE [App::Annotation] Text372
  LabelText = ESTA
  Position = (-9.75031e+07,-6.33302e+07,0)
FEATURE [App::Annotation] Text373
  LabelText = 26.35
  Position = (-9.75033e+07,-6.33306e+07,0)
FEATURE [App::Annotation] Text374
  LabelText = ESTA
  Position = (-9.74924e+07,-6.3328e+07,0)
FEATURE [App::Annotation] Text375
  LabelText = 26.65
  Position = (-9.74926e+07,-6.33284e+07,0)
FEATURE [App::Annotation] Text376
  LabelText = ESTA1
  Position = (-9.74896e+07,-6.33315e+07,0)
FEATURE [App::Annotation] Text377
  LabelText = 26.73
  Position = (-9.74897e+07,-6.33319e+07,0)
FEATURE [App::Annotation] Text378
  LabelText = ESTA
  Position = (-9.75049e+07,-6.33496e+07,0)
FEATURE [App::Annotation] Text379
  LabelText = 26.33
  Position = (-9.7505e+07,-6.335e+07,0)
FEATURE [App::Annotation] Text380
  LabelText = ESTA
  Position = (-9.75028e+07,-6.33394e+07,0)
FEATURE [App::Annotation] Text381
  LabelText = 26.38
  Position = (-9.7503e+07,-6.33398e+07,0)
FEATURE [App::Annotation] Text382
  LabelText = ESTA
  Position = (-9.74874e+07,-6.33358e+07,0)
FEATURE [App::Annotation] Text383
  LabelText = 26.82
  Position = (-9.74876e+07,-6.33362e+07,0)
FEATURE [App::Annotation] Text384
  LabelText = ESTA
  Position = (-9.74859e+07,-6.33402e+07,0)
FEATURE [App::Annotation] Text385
  LabelText = 26.85
  Position = (-9.74861e+07,-6.33406e+07,0)
FEATURE [App::Annotation] Text386
  LabelText = ESTA1
  Position = (-9.7487e+07,-6.33453e+07,0)
FEATURE [App::Annotation] Text387
  LabelText = 26.88
  Position = (-9.74871e+07,-6.33457e+07,0)
FEATURE [App::Annotation] Text388
  LabelText = ESTA
  Position = (-9.74752e+07,-6.33434e+07,0)
FEATURE [App::Annotation] Text389
  LabelText = 26.88
  Position = (-9.74753e+07,-6.33439e+07,0)
FEATURE [App::Annotation] Text390
  LabelText = ESTA
  Position = (-9.74803e+07,-6.33453e+07,0)
FEATURE [App::Annotation] Text391
  LabelText = 26.96
  Position = (-9.74805e+07,-6.33457e+07,0)
FEATURE [App::Annotation] Text392
  LabelText = ESTA
  Position = (-9.74849e+07,-6.33267e+07,0)
FEATURE [App::Annotation] Text393
  LabelText = 26.76
  Position = (-9.74851e+07,-6.33271e+07,0)
FEATURE [App::Annotation] Text394
  LabelText = ESTA
  Position = (-9.74808e+07,-6.33249e+07,0)
FEATURE [App::Annotation] Text395
  LabelText = 26.77
  Position = (-9.74809e+07,-6.33253e+07,0)
FEATURE [App::Annotation] Text396
  LabelText = LA
  Position = (-9.74935e+07,-6.33286e+07,0)
FEATURE [App::Annotation] Text397
  LabelText = 26.62
  Position = (-9.74942e+07,-6.33288e+07,0)
FEATURE [App::Annotation] Text398
  LabelText = LA
  Position = (-9.75015e+07,-6.33305e+07,0)
FEATURE [App::Annotation] Text399
  LabelText = CC
  Position = (-9.75017e+07,-6.33301e+07,0)
FEATURE [App::Annotation] Text400
  LabelText = 26.38
  Position = (-9.75024e+07,-6.33303e+07,0)
FEATURE [App::Annotation] Text401
  LabelText = CC
  Position = (-9.74973e+07,-6.3329e+07,0)
FEATURE [App::Annotation] Text402
  LabelText = 26.53
  Position = (-9.7498e+07,-6.33293e+07,0)
FEATURE [App::Annotation] Text403
  LabelText = CC
  Position = (-9.7491e+07,-6.3328e+07,0)
FEATURE [App::Annotation] Text404
  LabelText = 26.72
  Position = (-9.74917e+07,-6.33283e+07,0)
FEATURE [App::Annotation] Text405
  LabelText = VDCC
  Position = (-9.74806e+07,-6.33224e+07,0)
FEATURE [App::Annotation] Text406
  LabelText = 26.98
  Position = (-9.74813e+07,-6.3323e+07,0)
FEATURE [App::Annotation] Text407
  LabelText = VD
  Position = (-9.74788e+07,-6.33311e+07,0)
FEATURE [App::Annotation] Text408
  LabelText = 26.76
  Position = (-9.74794e+07,-6.33314e+07,0)
FEATURE [App::Annotation] Text409
  LabelText = VD
  Position = (-9.74778e+07,-6.33331e+07,0)
FEATURE [App::Annotation] Text410
  LabelText = 26.79
  Position = (-9.74785e+07,-6.33333e+07,0)
FEATURE [App::Annotation] Text411
  LabelText = VD
  Position = (-9.74762e+07,-6.33344e+07,0)
FEATURE [App::Annotation] Text412
  LabelText = 26.63
  Position = (-9.74769e+07,-6.33346e+07,0)
FEATURE [App::Annotation] Text413
  LabelText = CONTADOR
  Position = (-9.74801e+07,-6.33344e+07,0)
FEATURE [App::Annotation] Text414
  LabelText = 26.87
  Position = (-9.74807e+07,-6.33351e+07,0)
FEATURE [App::Annotation] Text415
  LabelText = EST
  Position = (-9.74739e+07,-6.33358e+07,0)
FEATURE [App::Annotation] Text416
  LabelText = 26.61
  Position = (-9.74742e+07,-6.33352e+07,0)
FEATURE [App::Annotation] Text417
  LabelText = CC1
  Position = (-9.74875e+07,-6.33497e+07,0)
FEATURE [App::Annotation] Text418
  LabelText = 26.84
  Position = (-9.74881e+07,-6.33501e+07,0)
FEATURE [App::Annotation] Text419
  LabelText = CC1
  Position = (-9.74951e+07,-6.33518e+07,0)
FEATURE [App::Annotation] Text420
  LabelText = 26.69
  Position = (-9.74955e+07,-6.3352e+07,0)
FEATURE [App::Annotation] Text421
  LabelText = CC1
  Position = (-9.74949e+07,-6.33803e+07,0)
FEATURE [App::Annotation] Text422
  LabelText = 26.53
  Position = (-9.74956e+07,-6.33807e+07,0)
FEATURE [App::Annotation] Text423
  LabelText = CC1
  Position = (-9.74931e+07,-6.33927e+07,0)
FEATURE [App::Annotation] Text424
  LabelText = 26.60
  Position = (-9.74936e+07,-6.3393e+07,0)
FEATURE [App::Annotation] Text425
  LabelText = CC
  Position = (-9.74967e+07,-6.33856e+07,0)
FEATURE [App::Annotation] Text426
  LabelText = 26.56
  Position = (-9.74974e+07,-6.33859e+07,0)
FEATURE [App::Annotation] Text427
  LabelText = EST
  Position = (-9.74989e+07,-6.33722e+07,0)
FEATURE [App::Annotation] Text428
  LabelText = 26.41
  Position = (-9.74991e+07,-6.33715e+07,0)
FEATURE [App::Annotation] Text429
  LabelText = EST
  Position = (-9.7506e+07,-6.33433e+07,0)
FEATURE [App::Annotation] Text430
  LabelText = 26.38
  Position = (-9.75062e+07,-6.33426e+07,0)
FEATURE [App::Annotation] Text431
  LabelText = 26.37
  Position = (-9.75059e+07,-6.33377e+07,0)
FEATURE [App::Annotation] Text432
  LabelText = CC17
  Position = (-9.74952e+07,-6.33756e+07,0)
FEATURE [App::Annotation] Text433
  LabelText = 26.48
  Position = (-9.74958e+07,-6.33761e+07,0)
FEATURE [App::Annotation] Text434
  LabelText = CC
  Position = (-9.75012e+07,-6.33733e+07,0)
FEATURE [App::Annotation] Text435
  LabelText = 26.34
  Position = (-9.75018e+07,-6.33736e+07,0)
FEATURE [App::Annotation] Text436
  LabelText = OL
  Position = (-9.75341e+07,-6.33344e+07,0)
FEATURE [App::Annotation] Text437
  LabelText = 26.31
  Position = (-9.75347e+07,-6.33347e+07,0)
FEATURE [App::Annotation] Text438
  LabelText = OL
  Position = (-9.75352e+07,-6.33395e+07,0)
FEATURE [App::Annotation] Text439
  LabelText = 26.40
  Position = (-9.75359e+07,-6.33397e+07,0)
FEATURE [App::Annotation] Text440
  LabelText = OL
  Position = (-9.75368e+07,-6.335e+07,0)
FEATURE [App::Annotation] Text441
  LabelText = 26.32
  Position = (-9.75375e+07,-6.33503e+07,0)
FEATURE [App::Annotation] Text442
  LabelText = OL
  Position = (-9.75384e+07,-6.33561e+07,0)
FEATURE [App::Annotation] Text443
  LabelText = 26.33
  Position = (-9.75391e+07,-6.33563e+07,0)
FEATURE [App::Annotation] Text444
  LabelText = OL
  Position = (-9.75397e+07,-6.33628e+07,0)
FEATURE [App::Annotation] Text445
  LabelText = 26.32
  Position = (-9.75404e+07,-6.3363e+07,0)
FEATURE [App::Annotation] Text446
  LabelText = OL
  Position = (-9.75413e+07,-6.33692e+07,0)
FEATURE [App::Annotation] Text447
  LabelText = 26.32
  Position = (-9.7542e+07,-6.33695e+07,0)
FEATURE [App::Annotation] Text448
  LabelText = OL
  Position = (-9.75436e+07,-6.3377e+07,0)
FEATURE [App::Annotation] Text449
  LabelText = 26.31
  Position = (-9.75442e+07,-6.33773e+07,0)
FEATURE [App::Annotation] Text450
  LabelText = EST
  Position = (-9.75417e+07,-6.3375e+07,0)
FEATURE [App::Annotation] Text451
  LabelText = LN
  Position = (-9.75355e+07,-6.33694e+07,0)
FEATURE [App::Annotation] Text452
  LabelText = 25.80
  Position = (-9.75362e+07,-6.33697e+07,0)
FEATURE [App::Annotation] Text453
  LabelText = EL
  Position = (-9.75339e+07,-6.33679e+07,0)
FEATURE [App::Annotation] Text454
  LabelText = 26.12
  Position = (-9.75346e+07,-6.33681e+07,0)
FEATURE [App::Annotation] Text455
  LabelText = IN
  Position = (-9.75341e+07,-6.33686e+07,0)
FEATURE [App::Annotation] Text456
  LabelText = 26.10
  Position = (-9.75347e+07,-6.33687e+07,0)
FEATURE [App::Annotation] Text457
  LabelText = MR30
  Position = (-9.75347e+07,-6.33683e+07,0)
FEATURE [App::Annotation] Text458
  LabelText = 25.89
  Position = (-9.75354e+07,-6.33689e+07,0)
FEATURE [App::Annotation] Text459
  LabelText = CC
  Position = (-9.75423e+07,-6.33759e+07,0)
FEATURE [App::Annotation] Text460
  LabelText = 26.01
  Position = (-9.75429e+07,-6.33761e+07,0)
FEATURE [App::Annotation] Text461
  LabelText = CC
  Position = (-9.75428e+07,-6.33768e+07,0)
FEATURE [App::Annotation] Text462
  LabelText = 25.98
  Position = (-9.75434e+07,-6.3377e+07,0)
FEATURE [App::Annotation] Text463
  LabelText = LN
  Position = (-9.75434e+07,-6.33787e+07,0)
FEATURE [App::Annotation] Text464
  LabelText = 25.75
  Position = (-9.75441e+07,-6.33789e+07,0)
FEATURE [App::Annotation] Text465
  LabelText = LN
  Position = (-9.75421e+07,-6.33784e+07,0)
FEATURE [App::Annotation] Text466
  LabelText = 25.75
  Position = (-9.75427e+07,-6.33786e+07,0)
FEATURE [App::Annotation] Text467
  LabelText = LN
  Position = (-9.75411e+07,-6.33776e+07,0)
FEATURE [App::Annotation] Text468
  LabelText = 25.75
  Position = (-9.75418e+07,-6.33778e+07,0)
FEATURE [App::Annotation] Text469
  LabelText = EST
  Position = (-9.75287e+07,-6.33165e+07,0)
FEATURE [App::Annotation] Text470
  LabelText = 25.63
  Position = (-9.75289e+07,-6.33172e+07,0)
FEATURE [App::Annotation] Text471
  LabelText = CXA
  Position = (-9.75259e+07,-6.33149e+07,0)
FEATURE [App::Annotation] Text472
  LabelText = 25.58
  Position = (-9.75262e+07,-6.33153e+07,0)
FEATURE [App::Annotation] Text473
  LabelText = CXA
  Position = (-9.75249e+07,-6.33171e+07,0)
FEATURE [App::Annotation] Text474
  LabelText = 25.67
  Position = (-9.75252e+07,-6.33175e+07,0)
FEATURE [App::Annotation] Text475
  LabelText = CXD
  Position = (-9.75267e+07,-6.33196e+07,0)
FEATURE [App::Annotation] Text476
  LabelText = 25.69
  Position = (-9.7527e+07,-6.33201e+07,0)
FEATURE [App::Annotation] Text477
  LabelText = VD
  Position = (-9.75251e+07,-6.33223e+07,0)
FEATURE [App::Annotation] Text478
  LabelText = 25.68
  Position = (-9.75258e+07,-6.33226e+07,0)
FEATURE [App::Annotation] Text479
  LabelText = CXD
  Position = (-9.75291e+07,-6.33237e+07,0)
FEATURE [App::Annotation] Text480
  LabelText = 25.71
  Position = (-9.75294e+07,-6.33241e+07,0)
FEATURE [App::Annotation] Text481
  LabelText = UM25
  Position = (-9.75314e+07,-6.33351e+07,0)
FEATURE [App::Annotation] Text482
  LabelText = 25.63
  Position = (-9.75321e+07,-6.33357e+07,0)
FEATURE [App::Annotation] Text483
  LabelText = UM25
  Position = (-9.75313e+07,-6.33344e+07,0)
FEATURE [App::Annotation] Text484
  LabelText = 25.62
  Position = (-9.75319e+07,-6.3335e+07,0)
FEATURE [App::Annotation] Text485
  LabelText = UM25
  Position = (-9.75284e+07,-6.33347e+07,0)
FEATURE [App::Annotation] Text486
  LabelText = 25.63
  Position = (-9.7529e+07,-6.33352e+07,0)
FEATURE [App::Annotation] Text487
  LabelText = UM25
  Position = (-9.75286e+07,-6.33353e+07,0)
FEATURE [App::Annotation] Text488
  LabelText = 25.63
  Position = (-9.75292e+07,-6.33358e+07,0)
FEATURE [App::Annotation] Text489
  LabelText = CXD
  Position = (-9.7531e+07,-6.33399e+07,0)
FEATURE [App::Annotation] Text490
  LabelText = 25.73
  Position = (-9.75313e+07,-6.33403e+07,0)
FEATURE [App::Annotation] Text491
  LabelText = CXA
  Position = (-9.75337e+07,-6.33483e+07,0)
FEATURE [App::Annotation] Text492
  LabelText = 25.74
  Position = (-9.7534e+07,-6.33488e+07,0)
FEATURE [App::Annotation] Text493
  LabelText = UM25
  Position = (-9.75346e+07,-6.33492e+07,0)
FEATURE [App::Annotation] Text494
  LabelText = 25.64
  Position = (-9.75352e+07,-6.33498e+07,0)
FEATURE [App::Annotation] Text495
  LabelText = UM25
  Position = (-9.75347e+07,-6.33498e+07,0)
FEATURE [App::Annotation] Text496
  LabelText = 25.65
  Position = (-9.75354e+07,-6.33504e+07,0)
FEATURE [App::Annotation] Text497
  LabelText = UM25
  Position = (-9.75319e+07,-6.33506e+07,0)
FEATURE [App::Annotation] Text498
  LabelText = 25.66
  Position = (-9.75325e+07,-6.33512e+07,0)
FEATURE [App::Annotation] Text499
  LabelText = UM25
  Position = (-9.75317e+07,-6.335e+07,0)
FEATURE [App::Annotation] Text500
  LabelText = 25.67
  Position = (-9.75324e+07,-6.33505e+07,0)
FEATURE [App::Annotation] Text501
  LabelText = VD
  Position = (-9.75314e+07,-6.33498e+07,0)
FEATURE [App::Annotation] Text502
  LabelText = 25.64
  Position = (-9.75321e+07,-6.335e+07,0)
FEATURE [App::Annotation] Text503
  LabelText = VD
  Position = (-9.75349e+07,-6.33655e+07,0)
FEATURE [App::Annotation] Text504
  LabelText = 25.75
  Position = (-9.75364e+07,-6.33657e+07,0)
FEATURE [App::Annotation] Text505
  LabelText = UM25
  Position = (-9.75352e+07,-6.33658e+07,0)
FEATURE [App::Annotation] Text506
  LabelText = 25.74
  Position = (-9.75358e+07,-6.33663e+07,0)
FEATURE [App::Annotation] Text507
  LabelText = UM25
  Position = (-9.75353e+07,-6.33664e+07,0)
FEATURE [App::Annotation] Text508
  LabelText = 25.74
  Position = (-9.7536e+07,-6.3367e+07,0)
FEATURE [App::Annotation] Text509
  LabelText = UM25
  Position = (-9.75381e+07,-6.33651e+07,0)
FEATURE [App::Annotation] Text510
  LabelText = 25.70
  Position = (-9.75387e+07,-6.33657e+07,0)
FEATURE [App::Annotation] Text511
  LabelText = UM25
  Position = (-9.75382e+07,-6.33658e+07,0)
FEATURE [App::Annotation] Text512
  LabelText = 25.70
  Position = (-9.75388e+07,-6.33663e+07,0)
FEATURE [App::Annotation] Text513
  LabelText = CXA
  Position = (-9.75394e+07,-6.3373e+07,0)
FEATURE [App::Annotation] Text514
  LabelText = 25.79
  Position = (-9.75397e+07,-6.33734e+07,0)
FEATURE [App::Annotation] Text515
  LabelText = UM25
  Position = (-9.75412e+07,-6.33778e+07,0)
FEATURE [App::Annotation] Text516
  LabelText = 25.71
  Position = (-9.75417e+07,-6.33784e+07,0)
FEATURE [App::Annotation] Text517
  LabelText = UM25
  Position = (-9.75417e+07,-6.33783e+07,0)
FEATURE [App::Annotation] Text518
  LabelText = 25.72
  Position = (-9.75423e+07,-6.33789e+07,0)
FEATURE [App::Annotation] Text519
  LabelText = CX
  Position = (-9.75411e+07,-6.33968e+07,0)
FEATURE [App::Annotation] Text520
  LabelText = 25.97
  Position = (-9.75415e+07,-6.33972e+07,0)
FEATURE [App::Annotation] Text521
  LabelText = CC
  Position = (-9.75383e+07,-6.33929e+07,0)
FEATURE [App::Annotation] Text522
  LabelText = 25.86
  Position = (-9.7539e+07,-6.33932e+07,0)
FEATURE [App::Annotation] Text523
  LabelText = CX
  Position = (-9.75414e+07,-6.3386e+07,0)
FEATURE [App::Annotation] Text524
  LabelText = 25.84
  Position = (-9.75419e+07,-6.33864e+07,0)
FEATURE [App::Annotation] Text525
  LabelText = OL
  Position = (-9.75374e+07,-6.33856e+07,0)
FEATURE [App::Annotation] Text526
  LabelText = 25.94
  Position = (-9.75381e+07,-6.33858e+07,0)
FEATURE [App::Annotation] Text527
  LabelText = CC
  Position = (-9.75459e+07,-6.33963e+07,0)
FEATURE [App::Annotation] Text528
  LabelText = 25.95
  Position = (-9.75466e+07,-6.33966e+07,0)
FEATURE [App::Annotation] Text529
  LabelText = LN
  Position = (-9.75463e+07,-6.33948e+07,0)
FEATURE [App::Annotation] Text530
  LabelText = 25.83
  Position = (-9.7547e+07,-6.3395e+07,0)
FEATURE [App::Annotation] Text531
  LabelText = LNS
  Position = (-9.75404e+07,-6.33928e+07,0)
FEATURE [App::Annotation] Text532
  LabelText = 25.87
  Position = (-9.75411e+07,-6.33932e+07,0)
FEATURE [App::Annotation] Text533
  LabelText = UM25
  Position = (-9.75392e+07,-6.33803e+07,0)
FEATURE [App::Annotation] Text534
  LabelText = 25.67
  Position = (-9.75398e+07,-6.33808e+07,0)
FEATURE [App::Annotation] Text535
  LabelText = UM25
  Position = (-9.75391e+07,-6.33796e+07,0)
FEATURE [App::Annotation] Text536
  LabelText = 25.67
  Position = (-9.75398e+07,-6.33801e+07,0)
FEATURE [App::Annotation] Text537
  LabelText = LN
  Position = (-9.75386e+07,-6.33793e+07,0)
FEATURE [App::Annotation] Text538
  LabelText = 25.76
  Position = (-9.75393e+07,-6.33795e+07,0)
FEATURE [App::Annotation] Text539
  LabelText = LN
  Position = (-9.75382e+07,-6.33783e+07,0)
FEATURE [App::Annotation] Text540
  LabelText = 25.81
  Position = (-9.75388e+07,-6.33786e+07,0)
FEATURE [App::Annotation] Text541
  LabelText = CCLN
  Position = (-9.75376e+07,-6.33772e+07,0)
FEATURE [App::Annotation] Text542
  LabelText = 25.83
  Position = (-9.75383e+07,-6.33777e+07,0)
FEATURE [App::Annotation] Text543
  LabelText = IN
  Position = (-9.75376e+07,-6.33773e+07,0)
FEATURE [App::Annotation] Text544
  LabelText = LN
  Position = (-9.75371e+07,-6.33769e+07,0)
FEATURE [App::Annotation] Text545
  LabelText = 25.82
  Position = (-9.75378e+07,-6.33772e+07,0)
FEATURE [App::Annotation] Text546
  LabelText = MR47
  Position = (-9.75365e+07,-6.33765e+07,0)
FEATURE [App::Annotation] Text547
  LabelText = 25.84
  Position = (-9.75367e+07,-6.33771e+07,0)
FEATURE [App::Annotation] Text548
  LabelText = CC
  Position = (-9.75353e+07,-6.33773e+07,0)
FEATURE [App::Annotation] Text549
  LabelText = CC
  Position = (-9.75295e+07,-6.33777e+07,0)
FEATURE [App::Annotation] Text550
  LabelText = 26.05
  Position = (-9.753e+07,-6.3378e+07,0)
FEATURE [App::Annotation] Text551
  LabelText = CC
  Position = (-9.75295e+07,-6.33769e+07,0)
FEATURE [App::Annotation] Text552
  LabelText = 26.04
  Position = (-9.75301e+07,-6.33772e+07,0)
FEATURE [App::Annotation] Text553
  LabelText = CC
  Position = (-9.75279e+07,-6.33768e+07,0)
FEATURE [App::Annotation] Text554
  LabelText = 26.04
  Position = (-9.75286e+07,-6.3377e+07,0)
FEATURE [App::Annotation] Text555
  LabelText = CC
  Position = (-9.75223e+07,-6.33771e+07,0)
FEATURE [App::Annotation] Text556
  LabelText = 26.05
  Position = (-9.75228e+07,-6.33773e+07,0)
FEATURE [App::Annotation] Text557
  LabelText = VDCC
  Position = (-9.75224e+07,-6.33759e+07,0)
FEATURE [App::Annotation] Text558
  LabelText = 26.10
  Position = (-9.7523e+07,-6.33764e+07,0)
FEATURE [App::Annotation] Text559
  LabelText = VD
  Position = (-9.75123e+07,-6.33737e+07,0)
FEATURE [App::Annotation] Text560
  LabelText = 26.22
  Position = (-9.75129e+07,-6.3374e+07,0)
FEATURE [App::Annotation] Text561
  LabelText = CC
  Position = (-9.75132e+07,-6.3374e+07,0)
FEATURE [App::Annotation] Text562
  LabelText = 26.20
  Position = (-9.75139e+07,-6.33742e+07,0)
FEATURE [App::Annotation] Text563
  LabelText = RUA FRANCISCO XAVIER DE MELO
  Position = (-9.75529e+07,-6.33302e+07,25667)
FEATURE [App::Annotation] Text564
  LabelText = RUA DOS CELEIROS STA.MARIA
  Position = (-9.7528e+07,-6.32978e+07,25667)
FEATURE [App::Annotation] Text565
  LabelText = RUA ROQUE FERREIRA LOBO
  Position = (-9.74884e+07,-6.32816e+07,25667)
FEATURE [App::Annotation] Text566
  LabelText = PRA?A MACHADO SANTOS
  Position = (-9.75324e+07,-6.34081e+07,25950)
FEATURE [App::Annotation] Text567
  LabelText = RUA JOS? EDUARDO C?SAR
  Position = (-9.74795e+07,-6.34012e+07,25950)
FEATURE [App::Annotation] Text568
  LabelText = sol.
  Position = (-9.74712e+07,-6.33398e+07,0)
FEATURE [App::Annotation] Text569
  LabelText = sol.
  Position = (-9.74721e+07,-6.33364e+07,0)
FEATURE [App::Annotation] Text570
  LabelText = sol.
  Position = (-9.74741e+07,-6.33287e+07,0)
FEATURE [App::Annotation] Text571
  LabelText = sol.
  Position = (-9.74748e+07,-6.33262e+07,0)
FEATURE [App::Annotation] Text572
  LabelText = sol.
  Position = (-9.74761e+07,-6.3321e+07,0)
FEATURE [App::Annotation] Text573
  LabelText = sol.
  Position = (-9.74732e+07,-6.3349e+07,0)
FEATURE [App::Annotation] Text574
  LabelText = sol.
  Position = (-9.74679e+07,-6.33491e+07,0)
FEATURE [App::Annotation] Text575
  LabelText = sol.
  Position = (-9.74685e+07,-6.33593e+07,0)
FEATURE [App::Annotation] Text576
  LabelText = sol.
  Position = (-9.74992e+07,-6.32994e+07,0)
FEATURE [App::Annotation] Text577
  LabelText = sol.
  Position = (-9.75063e+07,-6.33027e+07,0)
FEATURE [App::Annotation] Text578
  LabelText = sol.
  Position = (-9.75051e+07,-6.33019e+07,0)
FEATURE [App::Annotation] Text579
  LabelText = sol.
  Position = (-9.75164e+07,-6.33079e+07,0)
FEATURE [App::Annotation] Text580
  LabelText = sol.
  Position = (-9.75354e+07,-6.33181e+07,0)
FEATURE [App::Annotation] Text581
  LabelText = sol.
  Position = (-9.75368e+07,-6.33188e+07,0)
FEATURE [App::Annotation] Text582
  LabelText = sol.
  Position = (-9.75251e+07,-6.33127e+07,0)
FEATURE [App::Annotation] Text583
  LabelText = sol.
  Position = (-9.75333e+07,-6.33264e+07,0)
FEATURE [App::Annotation] Text584
  LabelText = sol.
  Position = (-9.75344e+07,-6.33342e+07,0)
FEATURE [App::Annotation] Text585
  LabelText = sol.
  Position = (-9.75355e+07,-6.33393e+07,0)
FEATURE [App::Annotation] Text586
  LabelText = sol.
  Position = (-9.75373e+07,-6.33498e+07,0)
FEATURE [App::Annotation] Text587
  LabelText = sol.
  Position = (-9.75387e+07,-6.33558e+07,0)
FEATURE [App::Annotation] Text588
  LabelText = sol.
  Position = (-9.75401e+07,-6.33625e+07,0)
FEATURE [App::Annotation] Text589
  LabelText = sol.
  Position = (-9.75416e+07,-6.3369e+07,0)
FEATURE [App::Annotation] Text590
  LabelText = sol.
  Position = (-9.75441e+07,-6.33768e+07,0)
FEATURE [App::Annotation] Text591
  LabelText = 1
  Position = (-9.75384e+07,-6.33771e+07,0)
FEATURE [App::Annotation] Text592
  LabelText = 2
  Position = (-9.75247e+07,-6.33245e+07,0)
FEATURE [App::Annotation] Text593
  LabelText = 3
  Position = (-9.75167e+07,-6.33149e+07,0)
FEATURE [App::Annotation] Text594
  LabelText = 4
  Position = (-9.75e+07,-6.33065e+07,0)
FEATURE [App::Annotation] Text595
  LabelText = 5
  Position = (-9.74979e+07,-6.33225e+07,0)
FEATURE [App::Annotation] Text596
  LabelText = 6
  Position = (-9.7504e+07,-6.33251e+07,0)
FEATURE [App::Annotation] Text597
  LabelText = 7
  Position = (-9.75028e+07,-6.33301e+07,0)
FEATURE [App::Annotation] Text598
  LabelText = 8
  Position = (-9.74908e+07,-6.33276e+07,0)
FEATURE [App::Annotation] Text599
  LabelText = 9
  Position = (-9.74909e+07,-6.33259e+07,0)
FEATURE [App::Annotation] Text600
  LabelText = 10
  Position = (-9.74789e+07,-6.33236e+07,0)
FEATURE [App::Annotation] Text601
  LabelText = 11
  Position = (-9.74735e+07,-6.3345e+07,0)
FEATURE [App::Annotation] Text602
  LabelText = 12
  Position = (-9.74964e+07,-6.33532e+07,0)
FEATURE [App::Annotation] Text603
  LabelText = 13
  Position = (-9.75009e+07,-6.33748e+07,0)
FEATURE [App::Annotation] Text604
  LabelText = sol.
  Position = (-9.75376e+07,-6.33853e+07,0)
FEATURE [App::Annotation] Text605
  LabelText = 14
  Position = (-9.75142e+07,-6.33736e+07,0)
FEATURE [App::Annotation] Text606
  LabelText = Antiga Casa Hip?lito
  Position = (314401,56114.9,0)
FEATURE [App::Annotation] Text607
  LabelText = Torres Vedras
  Position = (321944,49195.3,0)
FEATURE [App::Annotation] Text608
  LabelText = Escala 1:500
  Position = (323553,19226.1,0)
FEATURE [App::Annotation] Text609
  LabelText = 2002
  Position = (333363,12993.3,0)
FEATURE [App::Annotation] Text610
  LabelText = Planta de Localiza??o
  Position = (312374,26727,0)
FEATURE [Part::Feature] ENTITIES_CAIXAS_DE_VISITA
  shape: bbox 76470 x 104400 x 2e-07 mm, 0 faces, 0 solids (baked)
FEATURE [Part::Feature] ENTITIES_CAIXAS_DIVERSAS_ELECT_E_TELEC__
  shape: bbox 60800 x 26520 x 2e-07 mm, 0 faces, 0 solids (baked)
FEATURE [Part::Feature] ENTITIES_DEGRAUS
  shape: bbox 12350 x 3383 x 2e-07 mm, 0 faces, 0 solids (baked)
FEATURE [Part::Feature] ENTITIES_ESTACIONAMENTOS
  shape: bbox 59010 x 63050 x 2e-07 mm, 0 faces, 0 solids (baked)
FEATURE [Part::Feature] ENTITIES_ESTACOES
  shape: bbox 68020 x 64590 x 2e-07 mm, 0 faces, 0 solids (baked)
FEATURE [Part::Feature] ENTITIES_HATCH
  shape: bbox 100400 x 110500 x 2e-07 mm, 0 faces, 0 solids (baked)
FEATURE [Part::Feature] ENTITIES_LANCIS
  shape: bbox 90170 x 116100 x 2e-07 mm, 0 faces, 0 solids (baked)
FEATURE [Part::Feature] ENTITIES_MALHA_DE_COORDENADAS
  shape: bbox 155000 x 105000 x 2e-07 mm, 0 faces, 0 solids (baked)
FEATURE [Part::Feature] ENTITIES_MUROS
  shape: bbox 6523 x 3774 x 2e-07 mm, 0 faces, 0 solids (baked)
FEATURE [Part::Feature] ENTITIES_PINOS
  shape: bbox 41630 x 29570 x 2e-07 mm, 0 faces, 0 solids (baked)
FEATURE [Part::Feature] ENTITIES_RAMPA
  shape: bbox 7683 x 5072 x 2e-07 mm, 0 faces, 0 solids (baked)
FEATURE [Part::Feature] ENTITIES_SUMIDOUROS
  shape: bbox 70950 x 80960 x 2e-07 mm, 0 faces, 0 solids (baked)
FEATURE [Part::Feature] ENTITIES_TALUDES
  shape: bbox 10170 x 13920 x 2e-07 mm, 0 faces, 0 solids (baked)
FEATURE [Part::Feature] ENTITIES_TOPONIMIA
  shape: bbox 9405 x 7785 x 2e-07 mm, 0 faces, 0 solids (baked)
FEATURE [Part::Feature] ENTITIES_VEDA__ES
  shape: bbox 46580 x 74580 x 2e-07 mm, 0 faces, 0 solids (baked)
FEATURE [Part::Feature] ENTITIES_ZIGUEZAGUES
  shape: bbox 21980 x 11910 x 2e-07 mm, 0 faces, 0 solids (baked)
FEATURE [Part::Feature] ENTITIES___REA_INTERVEN__O
  shape: bbox 63760 x 86960 x 2e-07 mm, 0 faces, 0 solids (baked)
FEATURE [Part::Feature] ENTITIES_pontos
  shape: bbox 89790 x 99440 x 2e-07 mm, 0 faces, 0 solids (baked)
FEATURE [App::DocumentObjectGroup] Group  label="Textos"
  Group = -> [Text610,Text002,Text011,Text012,Text003,Text010,Text071,Text100,Text101,Text160,Text161,Text162,Text163,Text166,Text164,Text165,Text167,Text131,Text132,Text133,Text134,Text098,Text099,Text066,Text103,Text104,Text074,Text062,Text029,Text023,Text035,Text053,Text037,Text004,Text028,Text085,Text086,Text017,Text001,Text146,Text145,Text147,Text150,Text148,Text009,Text016,Text038,Text025,Text092,Text093,+561 more]
FEATURE [Part::Feature] Edge
  shape: bbox 2385 x 10100 x 2e-07 mm, 0 faces, 0 solids (baked)
FEATURE [Part::Feature] Edge001
  shape: bbox 1086 x 6907 x 2e-07 mm, 0 faces, 0 solids (baked)
FEATURE [Part::Feature] Edge002
  shape: bbox 5802 x 1529 x 2e-07 mm, 0 faces, 0 solids (baked)
FEATURE [Part::Feature] Edge003
  shape: bbox 7344 x 1734 x 2e-07 mm, 0 faces, 0 solids (baked)
FEATURE [Part::Feature] Edge004
  shape: bbox 6814 x 1603 x 2e-07 mm, 0 faces, 0 solids (baked)
FEATURE [Part::Feature] Edge005
  shape: bbox 9774 x 1536 x 2e-07 mm, 0 faces, 0 solids (baked)
FEATURE [Part::Feature] Edge006
  shape: bbox 8122 x 1563 x 2e-07 mm, 0 faces, 0 solids (baked)
FEATURE [Part::Feature] Edge007
  shape: bbox 1607 x 6805 x 2e-07 mm, 0 faces, 0 solids (baked)
FEATURE [Part::Feature] Edge008
  shape: bbox 1360 x 5781 x 2e-07 mm, 0 faces, 0 solids (baked)
FEATURE [Part::Feature] Edge010
  shape: bbox 634.1 x 329.4 x 2e-07 mm, 0 faces, 0 solids (baked)
FEATURE [Part::Feature] Edge012
  shape: bbox 5803 x 1528 x 2e-07 mm, 0 faces, 0 solids (baked)
FEATURE [Part::Feature] Edge013
  shape: bbox 5792 x 1565 x 2e-07 mm, 0 faces, 0 solids (baked)
FEATURE [Part::Feature] Edge026
  shape: bbox 6952 x 819.5 x 2e-07 mm, 0 faces, 0 solids (baked)
FEATURE [Part::Feature] Edge027
  shape: bbox 16110 x 6200 x 2e-07 mm, 0 faces, 0 solids (baked)
FEATURE [Part::Feature] Edge028
  shape: bbox 1469 x 12460 x 2e-07 mm, 0 faces, 0 solids (baked)
FEATURE [Part::Feature] Edge029
  shape: bbox 12500 x 2858 x 2e-07 mm, 0 faces, 0 solids (baked)
FEATURE [Part::Feature] Edge030
  shape: bbox 3072 x 1471 x 2e-07 mm, 0 faces, 0 solids (baked)
FEATURE [Part::Feature] Edge031
  shape: bbox 7027 x 3877 x 2e-07 mm, 0 faces, 0 solids (baked)
FEATURE [Part::Feature] Edge032
  shape: bbox 10110 x 4758 x 2e-07 mm, 0 faces, 0 solids (baked)
FEATURE [Part::Feature] Edge033
  shape: bbox 3548 x 9794 x 2e-07 mm, 0 faces, 0 solids (baked)
FEATURE [Part::Feature] Edge034
  shape: bbox 4015 x 8529 x 2e-07 mm, 0 faces, 0 solids (baked)
FEATURE [Part::Feature] Edge035
  shape: bbox 4347 x 7880 x 2e-07 mm, 0 faces, 0 solids (baked)
FEATURE [Part::Feature] Edge036
  shape: bbox 1549 x 4023 x 2e-07 mm, 0 faces, 0 solids (baked)
FEATURE [Part::Feature] Edge037
  shape: bbox 1962 x 5329 x 2e-07 mm, 0 faces, 0 solids (baked)
FEATURE [Part::Feature] Edge038
  shape: bbox 15130 x 6811 x 2e-07 mm, 0 faces, 0 solids (baked)
FEATURE [Part::Feature] Edge039
  shape: bbox 11310 x 5144 x 2e-07 mm, 0 faces, 0 solids (baked)
FEATURE [Part::Feature] Edge040
  shape: bbox 4485 x 9963 x 2e-07 mm, 0 faces, 0 solids (baked)
FEATURE [Part::Feature] Edge041
  shape: bbox 5700 x 1259 x 2e-07 mm, 0 faces, 0 solids (baked)
FEATURE [Part::Feature] Edge042
  shape: bbox 2897 x 6373 x 2e-07 mm, 0 faces, 0 solids (baked)
FEATURE [Part::Feature] Edge043
  shape: bbox 5605 x 2143 x 2e-07 mm, 0 faces, 0 solids (baked)
FEATURE [Part::Feature] Edge044
  shape: bbox 4669 x 3769 x 2e-07 mm, 0 faces, 0 solids (baked)
FEATURE [Part::Feature] Edge045
  shape: bbox 9577 x 106.6 x 2e-07 mm, 0 faces, 0 solids (baked)
FEATURE [Part::Feature] Edge046
  shape: bbox 7410 x 9179 x 2e-07 mm, 0 faces, 0 solids (baked)
FEATURE [Part::Feature] Edge047
  shape: bbox 6182 x 16170 x 2e-07 mm, 0 faces, 0 solids (baked)
FEATURE [Part::Feature] Edge048
  shape: bbox 2745 x 10160 x 2e-07 mm, 0 faces, 0 solids (baked)
FEATURE [Part::Feature] Edge049
  shape: bbox 3736 x 14180 x 2e-07 mm, 0 faces, 0 solids (baked)
FEATURE [Part::Feature] Edge050
  shape: bbox 2564 x 9809 x 2e-07 mm, 0 faces, 0 solids (baked)
FEATURE [Part::Feature] Edge051
  shape: bbox 1413 x 1730 x 2e-07 mm, 0 faces, 0 solids (baked)
FEATURE [Part::Feature] Edge052
  shape: bbox 10640 x 408.6 x 2e-07 mm, 0 faces, 0 solids (baked)
FEATURE [Part::Feature] Edge053
  shape: bbox 3094 x 6833 x 2e-07 mm, 0 faces, 0 solids (baked)
FEATURE [Part::Feature] Edge054
  shape: bbox 4990 x 313.3 x 2e-07 mm, 0 faces, 0 solids (baked)
FEATURE [Part::Feature] Edge055
  shape: bbox 3493 x 7679 x 2e-07 mm, 0 faces, 0 solids (baked)
FEATURE [Part::Feature] Edge056
  shape: bbox 3552 x 7845 x 2e-07 mm, 0 faces, 0 solids (baked)
FEATURE [Part::Feature] Edge057
  shape: bbox 16240 x 2919 x 2e-07 mm, 0 faces, 0 solids (baked)
FEATURE [Part::Feature] Edge058
  shape: bbox 113.4 x 1487 x 2e-07 mm, 0 faces, 0 solids (baked)
FEATURE [Part::Feature] Edge059
  shape: bbox 600 x 9558 x 2e-07 mm, 0 faces, 0 solids (baked)
FEATURE [Part::Feature] Edge060
  shape: bbox 1610 x 186.6 x 2e-07 mm, 0 faces, 0 solids (baked)
FEATURE [Part::Feature] Edge061
  shape: bbox 722.9 x 15880 x 2e-07 mm, 0 faces, 0 solids (baked)
FEATURE [Part::Feature] Edge062
  shape: bbox 10470 x 671 x 2e-07 mm, 0 faces, 0 solids (baked)
FEATURE [Part::Feature] Edge063
  shape: bbox 10770 x 687.6 x 2e-07 mm, 0 faces, 0 solids (baked)
FEATURE [Part::Feature] Edge064
  shape: bbox 100.1 x 6.481 x 2e-07 mm, 0 faces, 0 solids (baked)
FEATURE [Part::Feature] Edge065
  shape: bbox 5738 x 1482 x 2e-07 mm, 0 faces, 0 solids (baked)
FEATURE [Part::Feature] Edge066
  shape: bbox 623.7 x 7481 x 2e-07 mm, 0 faces, 0 solids (baked)
FEATURE [Part::Feature] Edge067
  shape: bbox 414.6 x 6224 x 2e-07 mm, 0 faces, 0 solids (baked)
FEATURE [Part::Feature] Edge068
  shape: bbox 4818 x 833.2 x 2e-07 mm, 0 faces, 0 solids (baked)
FEATURE [Part::Feature] Edge069
  shape: bbox 1400 x 41.25 x 2e-07 mm, 0 faces, 0 solids (baked)
FEATURE [Part::Feature] Edge070
  shape: bbox 143.2 x 4818 x 2e-07 mm, 0 faces, 0 solids (baked)
FEATURE [Part::Feature] Edge071
  shape: bbox 5417 x 417.8 x 2e-07 mm, 0 faces, 0 solids (baked)
FEATURE [Part::Feature] Edge072
  shape: bbox 104.4 x 4296 x 2e-07 mm, 0 faces, 0 solids (baked)
FEATURE [Part::Feature] Edge073
  shape: bbox 1234 x 145.5 x 2e-07 mm, 0 faces, 0 solids (baked)
FEATURE [Part::Feature] Edge074
  shape: bbox 286.3 x 5515 x 2e-07 mm, 0 faces, 0 solids (baked)
FEATURE [Part::Feature] Edge075
  shape: bbox 348.2 x 7368 x 2e-07 mm, 0 faces, 0 solids (baked)
FEATURE [Part::Feature] Edge076
  shape: bbox 9577 x 92.62 x 2e-07 mm, 0 faces, 0 solids (baked)
FEATURE [Part::Feature] Edge077
  shape: bbox 2457 x 9569 x 2e-07 mm, 0 faces, 0 solids (baked)
FEATURE [Part::Feature] Edge078
  shape: bbox 9577 x 92.62 x 2e-07 mm, 0 faces, 0 solids (baked)
FEATURE [Part::Feature] Edge079
  shape: bbox 1880 x 53.56 x 2e-07 mm, 0 faces, 0 solids (baked)
FEATURE [Part::Feature] Edge080
  shape: bbox 183.7 x 19120 x 2e-07 mm, 0 faces, 0 solids (baked)
FEATURE [Part::Feature] Edge081
  shape: bbox 75.03 x 7968 x 2e-07 mm, 0 faces, 0 solids (baked)
FEATURE [Part::Feature] Edge082
  shape: bbox 230.9 x 20820 x 2e-07 mm, 0 faces, 0 solids (baked)
FEATURE [Part::Feature] Edge083
  shape: bbox 1876 x 2321 x 2e-07 mm, 0 faces, 0 solids (baked)
FEATURE [Part::Feature] Edge084
  shape: bbox 7040 x 1250 x 2e-07 mm, 0 faces, 0 solids (baked)
FEATURE [Part::Feature] Edge085
  shape: bbox 425.9 x 1659 x 2e-07 mm, 0 faces, 0 solids (baked)
FEATURE [Part::Feature] Edge086
  shape: bbox 5893 x 1048 x 2e-07 mm, 0 faces, 0 solids (baked)
FEATURE [Part::Feature] Edge087
  shape: bbox 4815 x 6080 x 2e-07 mm, 0 faces, 0 solids (baked)
FEATURE [Part::Feature] Edge088
  shape: bbox 302.3 x 7493 x 2e-07 mm, 0 faces, 0 solids (baked)
FEATURE [Part::Feature] Edge089
  shape: bbox 3173 x 195.8 x 2e-07 mm, 0 faces, 0 solids (baked)
FEATURE [Part::Feature] Edge090
  shape: bbox 15790 x 3866 x 2e-07 mm, 0 faces, 0 solids (baked)
FEATURE [Part::Feature] Edge091
  shape: bbox 3738 x 8260 x 2e-07 mm, 0 faces, 0 solids (baked)
FEATURE [Part::Feature] Edge092
  shape: bbox 15780 x 3931 x 2e-07 mm, 0 faces, 0 solids (baked)
FEATURE [Part::Feature] Edge093
  shape: bbox 641.6 x 12410 x 2e-07 mm, 0 faces, 0 solids (baked)
FEATURE [Part::Feature] Edge094
  shape: bbox 12060 x 571.4 x 2e-07 mm, 0 faces, 0 solids (baked)
FEATURE [Part::Feature] Edge095
  shape: bbox 48.76 x 740.8 x 2e-07 mm, 0 faces, 0 solids (baked)
FEATURE [Part::Feature] Edge096
  shape: bbox 1864 x 271.7 x 2e-07 mm, 0 faces, 0 solids (baked)
FEATURE [Part::Feature] Edge097
  shape: bbox 80.56 x 843.7 x 2e-07 mm, 0 faces, 0 solids (baked)
FEATURE [Part::Feature] Edge098
  shape: bbox 1620 x 154.8 x 2e-07 mm, 0 faces, 0 solids (baked)
FEATURE [Part::Feature] Edge099
  shape: bbox 80.67 x 843.2 x 2e-07 mm, 0 faces, 0 solids (baked)
FEATURE [Part::Feature] Edge100
  shape: bbox 54.17 x 647.9 x 2e-07 mm, 0 faces, 0 solids (baked)
FEATURE [Part::Feature] Edge101
  shape: bbox 51.63 x 617.9 x 2e-07 mm, 0 faces, 0 solids (baked)
FEATURE [Part::Feature] Edge102
  shape: bbox 1508 x 127.1 x 2e-07 mm, 0 faces, 0 solids (baked)
FEATURE [Part::Feature] Edge103
  shape: bbox 33.68 x 745.6 x 2e-07 mm, 0 faces, 0 solids (baked)
FEATURE [Part::Feature] Edge104
  shape: bbox 32.14 x 715.6 x 2e-07 mm, 0 faces, 0 solids (baked)
FEATURE [Part::Feature] Edge105
  shape: bbox 1512 x 68.05 x 2e-07 mm, 0 faces, 0 solids (baked)
FEATURE [Part::Feature] Edge106
  shape: bbox 14490 x 1380 x 2e-07 mm, 0 faces, 0 solids (baked)
FEATURE [Part::Feature] Edge107
  shape: bbox 1500 x 149.1 x 2e-07 mm, 0 faces, 0 solids (baked)
FEATURE [Part::Feature] Edge108
  shape: bbox 6638 x 459.3 x 2e-07 mm, 0 faces, 0 solids (baked)
FEATURE [Part::Feature] Edge109
  shape: bbox 38.02 x 791.5 x 2e-07 mm, 0 faces, 0 solids (baked)
FEATURE [Part::Feature] Edge110
  shape: bbox 638.4 x 18.31 x 2e-07 mm, 0 faces, 0 solids (baked)
FEATURE [Part::Feature] Edge111
  shape: bbox 5229 x 885.5 x 2e-07 mm, 0 faces, 0 solids (baked)
FEATURE [Part::Feature] Edge112
  shape: bbox 15290 x 8235 x 2e-07 mm, 0 faces, 0 solids (baked)
FEATURE [Part::Feature] Edge113
  shape: bbox 1437 x 2554 x 2e-07 mm, 0 faces, 0 solids (baked)
FEATURE [Part::Feature] Edge114
  shape: bbox 4295 x 19450 x 2e-07 mm, 0 faces, 0 solids (baked)
FEATURE [Part::Feature] Edge115
  shape: bbox 6595 x 29890 x 2e-07 mm, 0 faces, 0 solids (baked)
FEATURE [Part::Feature] Edge116
  shape: bbox 127.5 x 362.1 x 2e-07 mm, 0 faces, 0 solids (baked)
FEATURE [Part::Feature] Edge117
  shape: bbox 179.2 x 342.3 x 2e-07 mm, 0 faces, 0 solids (baked)
FEATURE [Part::Feature] Edge118
  shape: bbox 226.8 x 313.6 x 2e-07 mm, 0 faces, 0 solids (baked)
FEATURE [Part::Feature] Edge119
  shape: bbox 269.2 x 275.9 x 2e-07 mm, 0 faces, 0 solids (baked)
FEATURE [Part::Feature] Edge120
  shape: bbox 235.6 x 168.4 x 2e-07 mm, 0 faces, 0 solids (baked)
FEATURE [Part::Feature] Edge121
  shape: bbox 268.9 x 120.9 x 2e-07 mm, 0 faces, 0 solids (baked)
FEATURE [Part::Feature] Edge122
  shape: bbox 287.1 x 68.65 x 2e-07 mm, 0 faces, 0 solids (baked)
FEATURE [Part::Feature] Edge123
  shape: bbox 290.2 x 12.6 x 2e-07 mm, 0 faces, 0 solids (baked)
FEATURE [Part::Feature] Edge124
  shape: bbox 9991 x 480.4 x 2e-07 mm, 0 faces, 0 solids (baked)
FEATURE [Part::Feature] Edge125
  shape: bbox 134.3 x 2876 x 2e-07 mm, 0 faces, 0 solids (baked)
FEATURE [Part::Feature] Edge126
  shape: bbox 24830 x 637.1 x 2e-07 mm, 0 faces, 0 solids (baked)
FEATURE [Part::Feature] Edge127
  shape: bbox 122.4 x 15900 x 2e-07 mm, 0 faces, 0 solids (baked)
FEATURE [Part::Feature] Edge128
  shape: bbox 10050 x 608.4 x 2e-07 mm, 0 faces, 0 solids (baked)
FEATURE [Part::Feature] Edge129
  shape: bbox 7019 x 283.5 x 2e-07 mm, 0 faces, 0 solids (baked)
FEATURE [Part::Feature] Edge130
  shape: bbox 157.8 x 3376 x 2e-07 mm, 0 faces, 0 solids (baked)
FEATURE [Part::Feature] Edge131
  shape: bbox 23.42 x 499.4 x 2e-07 mm, 0 faces, 0 solids (baked)
FEATURE [Part::Feature] Edge132
  shape: bbox 121.3 x 15890 x 2e-07 mm, 0 faces, 0 solids (baked)
FEATURE [Part::Feature] Edge133
  shape: bbox 21910 x 1424 x 2e-07 mm, 0 faces, 0 solids (baked)
FEATURE [Part::Feature] Edge134
  shape: bbox 23.42 x 499.4 x 2e-07 mm, 0 faces, 0 solids (baked)
FEATURE [Part::Feature] Edge135
  shape: bbox 5037 x 235.6 x 2e-07 mm, 0 faces, 0 solids (baked)
FEATURE [Part::Feature] Edge136
  shape: bbox 737.3 x 15490 x 2e-07 mm, 0 faces, 0 solids (baked)
FEATURE [Part::Feature] Edge137
  shape: bbox 933.5 x 26.83 x 2e-07 mm, 0 faces, 0 solids (baked)
FEATURE [Part::Feature] Edge138
  shape: bbox 11990 x 2859 x 2e-07 mm, 0 faces, 0 solids (baked)
FEATURE [Part::Feature] Edge139
  shape: bbox 2481 x 10400 x 2e-07 mm, 0 faces, 0 solids (baked)
FEATURE [Part::Feature] Edge140
  shape: bbox 12290 x 986.7 x 2e-07 mm, 0 faces, 0 solids (baked)
FEATURE [Part::Feature] Edge141
  shape: bbox 60.1 x 4563 x 2e-07 mm, 0 faces, 0 solids (baked)
FEATURE [Part::Feature] Edge142
  shape: bbox 169.8 x 8.579 x 2e-07 mm, 0 faces, 0 solids (baked)
FEATURE [Part::Feature] Edge143
  shape: bbox 12830 x 3327 x 2e-07 mm, 0 faces, 0 solids (baked)
FEATURE [Part::Feature] Edge144
  shape: bbox 1298 x 418.4 x 2e-07 mm, 0 faces, 0 solids (baked)
FEATURE [Part::Feature] Edge145
  shape: bbox 191.4 x 896.4 x 2e-07 mm, 0 faces, 0 solids (baked)
FEATURE [Part::Feature] Edge150
  shape: bbox 78.83 x 793 x 2e-07 mm, 0 faces, 0 solids (baked)
FEATURE [Part::Feature] Edge151
  shape: bbox 75.58 x 793.6 x 2e-07 mm, 0 faces, 0 solids (baked)
FEATURE [Part::Feature] Edge152
  shape: bbox 1646 x 481 x 2e-07 mm, 0 faces, 0 solids (baked)
FEATURE [Part::Feature] Edge154
  shape: bbox 3813 x 164.8 x 2e-07 mm, 0 faces, 0 solids (baked)
FEATURE [Part::Feature] Edge155
  shape: bbox 612 x 7741 x 2e-07 mm, 0 faces, 0 solids (baked)
FEATURE [Part::Feature] Edge156
  shape: bbox 120.5 x 1368 x 2e-07 mm, 0 faces, 0 solids (baked)
FEATURE [Part::Feature] Wire
  shape: bbox 24000 x 27010 x 2e-07 mm, 0 faces, 0 solids (baked)
FEATURE [Part::Extrusion] Extrude
  Base = -> Wire
  Dir = (0,0,8500)
  Placement = pos=(0,0,26225) rot=(0,0,1;0rad)
  Solid = true
FEATURE [Part::Part2DObjectPython] DWire  # Draft 2D object (typed FeaturePython)
  ChamferSize = 0
  Closed = true
  End = (-9.74853e+07,-6.33588e+07,0)
  FilletRadius = 0
  Length = 49453.9
  MakeFace = true
  Points = (4) [(-97488900,-63351100,0),(-97473100,-63347200,0),(-97469600,-63354900,0),(-97485300,-63358800,0)]
  Start = (-9.74889e+07,-6.33511e+07,0)
  Subdivisions = 0
FEATURE [Part::Extrusion] Extrude001
  Base = -> DWire
  Dir = (0,0,8430)
  Solid = true
FEATURE [Part::Part2DObjectPython] DWire001  # Draft 2D object (typed FeaturePython)
  ChamferSize = 0
  Closed = true
  End = (-9.7466e+07,-6.33627e+07,0)
  FilletRadius = 0
  Length = 54110.6
  MakeFace = true
  Points = (6) [(-97469600,-63354900,0),(-97485300,-63358800,0),(-97484900,-63367300,0),(-97482100,-63367100,0),(-97482300,-63365600,0),(-97466000,-63362700,0)]
  Start = (-9.74696e+07,-6.33549e+07,0)
  Subdivisions = 0
FEATURE [Part::Extrusion] Extrude002
  Base = -> DWire001
  Dir = (0,0,7750)
  Solid = true
FEATURE [Part::Part2DObjectPython] Line  # Draft 2D object (typed FeaturePython)
  ChamferSize = 0
  Closed = false
  End = (-9.74731e+07,-6.33472e+07,0)
  FilletRadius = 0
  Length = 24244
  MakeFace = true
  Points = (2) [(-97496600,-63353000,0),(-97473100,-63347200,0)]
  Start = (-9.74966e+07,-6.3353e+07,0)
  Subdivisions = 0
FEATURE [Part::Part2DObjectPython] DWire002  # Draft 2D object (typed FeaturePython)
  ChamferSize = 0
  Closed = true
  End = (-97484872,-63367292,0)
  FilletRadius = 0
  Length = 36959.4
  MakeFace = true
  Points = (7) [(-97485300,-63358800,0),(-97495400,-63359500,0),(-97495900,-63365700,0),(-97491000,-63366600,0),(-97489600,-63366600,0),(-97489700,-63367600,0),+1 more]
  Start = (-97485344,-63358800,0)
  Subdivisions = 0
FEATURE [Part::Extrusion] Extrude003
  Base = -> DWire002
  Dir = (0,0,6520)
  Solid = true
FEATURE [Part::Part2DObjectPython] DWire003  # Draft 2D object (typed FeaturePython)
  ChamferSize = 0
  Closed = true
  End = (-97489672,-63367592,0)
  FilletRadius = 0
  Length = 45697.6
  MakeFace = true
  Points = (10) [(-97482100,-63367100,0),(-97481500,-63376700,0),(-97483100,-63376900,0),(-97493900,-63377600,0),(-97494900,-63377600,0),(-97494900,-63376100,0),+4 more]
  Start = (-9.74821e+07,-6.33671e+07,0)
  Subdivisions = 0
FEATURE [Part::Extrusion] Extrude004
  Base = -> DWire003
  Dir = (0,0,6170)
  Solid = true
FEATURE [Part::Part2DObjectPython] DWire004  # Draft 2D object (typed FeaturePython)
  ChamferSize = 0
  Closed = true
  End = (-97485344,-63358800,0)
  FilletRadius = 0
  Length = 31816.6
  MakeFace = true
  Points = (4) [(-97488900,-63351100,0),(-97494900,-63352500,0),(-97495400,-63359500,0),(-97485300,-63358800,0)]
  Start = (-9.74889e+07,-6.33511e+07,0)
  Subdivisions = 0
FEATURE [Part::Extrusion] Extrude005
  Base = -> DWire004
  Dir = (0,0,4000)
  Solid = true
FEATURE [Part::Part2DObjectPython] DWire005  # Draft 2D object (typed FeaturePython)
  ChamferSize = 0
  Closed = true
  End = (-97494912,-63377564,0)
  FilletRadius = 0
  Length = 55546.6
  MakeFace = true
  Points = (8) [(-97483100,-63376900,0),(-97482400,-63392700,0),(-97492900,-63393400,0),(-97493200,-63386100,0),(-97493300,-63386100,0),(-97493600,-63380500,0),+2 more]
  Start = (-9.74831e+07,-6.33769e+07,0)
  Subdivisions = 0
FEATURE [Part::Extrusion] Extrude006
  Base = -> DWire005
  Dir = (0,0,7300)
  Solid = true
FEATURE [Part::Part2DObjectPython] DWire006  # Draft 2D object (typed FeaturePython)
  ChamferSize = 0
  Closed = true
  End = (-9.75005e+07,-6.3386e+07,0)
  FilletRadius = 0
  Length = 35123.7
  MakeFace = true
  Points = (5) [(-97496700,-63385900,0),(-97496100,-63393600,0),(-97506100,-63394200,0),(-97506400,-63386700,0),(-97500500,-63386000,0)]
  Start = (-9.74967e+07,-6.33859e+07,0)
  Subdivisions = 0
FEATURE [Part::Extrusion] Extrude007
  Base = -> DWire006
  Dir = (0,0,7100)
  Solid = true
FEATURE [Part::Part2DObjectPython] DWire008  label="DWire007"  # Draft 2D object (typed FeaturePython)
  ChamferSize = 0
  Closed = true
  End = (-9.75063e+07,-6.33897e+07,0)
  FilletRadius = 0
  Length = 23139.5
  MakeFace = true
  Points = (6) [(-97506100,-63394200,0),(-97513100,-63394500,0),(-97513300,-63391100,0),(-97511400,-63391000,0),(-97511400,-63389900,0),(-97506300,-63389700,0)]
  Start = (-9.75061e+07,-6.33942e+07,0)
  Subdivisions = 0
FEATURE [Part::Extrusion] Extrude008
  Base = -> DWire008
  Dir = (0,0,2760)
  Solid = true
FEATURE [Part::Part2DObjectPython] Line001  # Draft 2D object (typed FeaturePython)
  ChamferSize = 0
  Closed = false
  End = (-9.75114e+07,-6.3391e+07,0)
  FilletRadius = 0
  Length = 15572.9
  MakeFace = true
  Points = (2) [(-97511900,-63375400,0),(-97511400,-63391000,0)]
  Start = (-9.75119e+07,-6.33754e+07,0)
  Subdivisions = 0
FEATURE [Part::Part2DObjectPython] Line003  # Draft 2D object (typed FeaturePython)
  ChamferSize = 0
  Closed = false
  End = (-9.7513e+07,-6.33764e+07,0)
  FilletRadius = 0
  Length = 835.873
  MakeFace = true
  Points = (2) [(-97513100,-63375600,0),(-97513000,-63376400,0)]
  Start = (-9.75131e+07,-6.33756e+07,0)
  Subdivisions = 0
FEATURE [Part::Part2DObjectPython] DWire009  # Draft 2D object (typed FeaturePython)
  ChamferSize = 0
  Closed = true
  End = (-9.7536e+07,-6.33776e+07,25930)
  FilletRadius = 0
  Length = 91887.2
  MakeFace = true
  Points = (29) [(-97537600,-63377700,25930),(-97538300,-63393200,25930),(-97533300,-63392900,25930),(-97533300,-63392400,25930),(-97528900,-63392100,25930),+24 more]
  Start = (-9.75376e+07,-6.33777e+07,25930)
  Subdivisions = 0
FEATURE [Part::Extrusion] Extrude009
  Base = -> DWire009
  Dir = (0,0,16500)
  Solid = true
FEATURE [Part::Part2DObjectPython] DWire010  # Draft 2D object (typed FeaturePython)
  ChamferSize = 0
  Closed = true
  End = (-9.75114e+07,-6.33899e+07,0)
  FilletRadius = 0
  Length = 43362.5
  MakeFace = true
  Points = (7) [(-97511400,-63389900,0),(-97506300,-63389700,0),(-97506400,-63386700,0),(-97500500,-63386000,0),(-97500900,-63378400,0),(-97511800,-63379100,0),+1 more]
  Start = (-97511416,-63389872,0)
  Subdivisions = 0
FEATURE [Part::Extrusion] Extrude010
  Base = -> DWire010
  Dir = (0,0,8820)
  Solid = true
FEATURE [Part::Part2DObjectPython] DWire011  # Draft 2D object (typed FeaturePython)
  ChamferSize = 0
  Closed = true
  End = (-9.75119e+07,-6.33763e+07,0)
  FilletRadius = 0
  Length = 33918.9
  MakeFace = true
  Points = (6) [(-97513000,-63376400,0),(-97513200,-63374200,0),(-97501100,-63373600,0),(-97500900,-63378400,0),(-97511800,-63379100,0),(-97511900,-63376300,0)]
  Start = (-9.7513e+07,-6.33764e+07,0)
  Subdivisions = 0
FEATURE [Part::Extrusion] Extrude011
  Base = -> DWire011
  Dir = (0,0,6000)
  Solid = true
FEATURE [Part::Part2DObjectPython] DWire012  # Draft 2D object (typed FeaturePython)
  ChamferSize = 0
  Closed = true
  End = (-9.75467e+07,-6.33443e+07,0)
  FilletRadius = 0
  Length = 63079.3
  MakeFace = true
  Points = (6) [(-97548200,-63332700,0),(-97532900,-63324500,0),(-97531500,-63327000,0),(-97535700,-63346500,0),(-97541400,-63345200,0),(-97546700,-63344300,0)]
  Start = (-9.75482e+07,-6.33327e+07,0)
  Subdivisions = 0
FEATURE [Part::Extrusion] Extrude012
  Base = -> DWire012
  Dir = (0,0,12500)
  Solid = true
FEATURE [Part::Part2DObjectPython] DWire013  # Draft 2D object (typed FeaturePython)
  ChamferSize = 0
  Closed = true
  End = (-9.75414e+07,-6.33452e+07,0)
  FilletRadius = 0
  Length = 89463.2
  MakeFace = true
  Points = (13) [(-97535700,-63346500,0),(-97542300,-63376400,0),(-97542500,-63376700,0),(-97542700,-63377100,0),(-97542900,-63377400,0),(-97543100,-63377700,0),+7 more]
  Start = (-9.75357e+07,-6.33465e+07,0)
  Subdivisions = 0
FEATURE [Part::Extrusion] Extrude013
  Base = -> DWire013
  Dir = (0,0,8300)
  Solid = true
FEATURE [Part::Part2DObjectPython] DWire014  # Draft 2D object (typed FeaturePython)
  ChamferSize = 0
  Closed = true
  End = (-9.75146e+07,-6.32975e+07,0)
  FilletRadius = 0
  Length = 41273.8
  MakeFace = true
  Points = (4) [(-97524300,-63301000,0),(-97520700,-63310700,0),(-97510600,-63306000,0),(-97514600,-63297500,0)]
  Start = (-9.75243e+07,-6.3301e+07,0)
  Subdivisions = 0
FEATURE [Part::Extrusion] Extrude014
  Base = -> DWire014
  Dir = (0,0,6750)
  Solid = true
FEATURE [Part::Part2DObjectPython] DWire015  # Draft 2D object (typed FeaturePython)
  ChamferSize = 0
  Closed = true
  End = (-9.75079e+07,-6.32942e+07,0)
  FilletRadius = 0
  Length = 33883.5
  MakeFace = true
  Points = (4) [(-97514600,-63297500,0),(-97510600,-63306000,0),(-97503600,-63302100,0),(-97507900,-63294200,0)]
  Start = (-9.75146e+07,-6.32975e+07,0)
  Subdivisions = 0
FEATURE [Part::Extrusion] Extrude015
  Base = -> DWire015
  Dir = (0,0,8000)
  Solid = true
FEATURE [Part::Part2DObjectPython] DWire016  # Draft 2D object (typed FeaturePython)
  ChamferSize = 0
  Closed = true
  End = (-9.75273e+07,-6.33043e+07,0)
  FilletRadius = 0
  Length = 54768.5
  MakeFace = true
  Points = (5) [(-97543400,-63310500,0),(-97539000,-63320500,0),(-97523800,-63313700,0),(-97525800,-63308300,0),(-97527300,-63304300,0)]
  Start = (-9.75434e+07,-6.33105e+07,0)
  Subdivisions = 0
FEATURE [Part::Extrusion] Extrude016
  Base = -> DWire016
  Dir = (0,0,8000)
  Solid = true
FEATURE [Part::Part2DObjectPython] DWire017  # Draft 2D object (typed FeaturePython)
  ChamferSize = 0
  Closed = true
  End = (-9.75023e+07,-6.32929e+07,0)
  FilletRadius = 0
  Length = 26109.7
  MakeFace = true
  Points = (4) [(-97507900,-63294200,0),(-97503600,-63302100,0),(-97500500,-63300600,0),(-97502300,-63292900,0)]
  Start = (-9.75079e+07,-6.32942e+07,0)
  Subdivisions = 0
FEATURE [Part::Extrusion] Extrude017
  Base = -> DWire017
  Dir = (0,0,11000)
  Solid = true
FEATURE [Part::Feature] Edge009
  shape: bbox 1762 x 7703 x 25000 mm, 0 faces, 0 solids (baked)
FEATURE [App::DocumentObjectGroup] Group002  label="construcoes"
  Group = -> [Edge,Edge005,Edge004,Edge013,Edge002,Edge008,Edge012,Edge001,Edge010,Edge006,Edge007,Edge003,Edge009,Edge044,Edge045,Edge046,Edge047,Edge048,Edge049,Edge050,Edge051,Edge052,Edge053,Edge054,Edge055,Edge056,Edge057,Edge058,Edge073,Edge059,Edge060,Edge061,Edge062,Edge063,Edge064,Edge065,Edge066,Edge067,Edge068,Edge069,Edge070,Edge071,Edge072,Edge089,Edge074,Edge075,Edge076,Edge077,Edge078,Edge079,+89 more]
FEATURE [App::DocumentObjectGroup] Group001  label="levantamento"
  Group = -> [ENTITIES_pontos,ENTITIES_CAIXAS_DE_VISITA,ENTITIES_CAIXAS_DIVERSAS_ELECT_E_TELEC__,ENTITIES_DEGRAUS,ENTITIES_ESTACIONAMENTOS,ENTITIES_ESTACOES,ENTITIES_HATCH,ENTITIES_PINOS,ENTITIES_RAMPA,ENTITIES_MUROS,ENTITIES_LANCIS,ENTITIES_MALHA_DE_COORDENADAS,ENTITIES_SUMIDOUROS,ENTITIES_TALUDES,ENTITIES_TOPONIMIA,ENTITIES_VEDA__ES,ENTITIES_ZIGUEZAGUES,ENTITIES___REA_INTERVEN__O,Group002]
FEATURE [Part::Part2DObjectPython] DWire019  # Draft 2D object (typed FeaturePython)
  ChamferSize = 0
  Closed = true
  End = (-9.75023e+07,-6.32929e+07,0)
  FilletRadius = 0
  Length = 22647
  MakeFace = true
  Points = (4) [(-97500500,-63300600,0),(-97497200,-63299900,0),(-97498900,-63292200,0),(-97502300,-63292900,0)]
  Start = (-9.75005e+07,-6.33006e+07,0)
  Subdivisions = 0
FEATURE [Part::Extrusion] Extrude018
  Base = -> DWire019
  Dir = (0,0,13500)
  Solid = true
FEATURE [Part::Part2DObjectPython] DWire020  # Draft 2D object (typed FeaturePython)
  ChamferSize = 0
  Closed = true
  End = (-9.74964e+07,-6.32861e+07,0)
  FilletRadius = 0
  Length = 43333
  MakeFace = true
  Points = (5) [(-97498900,-63292200,0),(-97497200,-63299900,0),(-97488000,-63297800,0),(-97489500,-63285300,0),(-97496400,-63286100,0)]
  Start = (-9.74989e+07,-6.32922e+07,0)
  Subdivisions = 0
FEATURE [Part::Extrusion] Extrusion
  Base = -> DWire020
  Dir = (0,0,10950)
  Solid = true
FEATURE [Part::Part2DObjectPython] DWire021  # Draft 2D object (typed FeaturePython)
  ChamferSize = 0
  Closed = true
  End = (-9.74768e+07,-6.32896e+07,0)
  FilletRadius = 0
  Length = 33189.6
  MakeFace = true
  Points = (4) [(-97484100,-63291300,0),(-97482500,-63298100,0),(-97474400,-63299700,0),(-97476800,-63289600,0)]
  Start = (-9.74841e+07,-6.32913e+07,0)
  Subdivisions = 0
FEATURE [Part::Part2DObjectPython] DWire022  # Draft 2D object (typed FeaturePython)
  ChamferSize = 0
  Closed = true
  End = (-9.74635e+07,-6.32943e+07,0)
  FilletRadius = 0
  Length = 41331.1
  MakeFace = true
  Points = (4) [(-97476800,-63289600,0),(-97474400,-63299700,0),(-97464600,-63301200,0),(-97463500,-63294300,0)]
  Start = (-9.74768e+07,-6.32896e+07,0)
  Subdivisions = 0
FEATURE [Part::Part2DObjectPython] DWire023  # Draft 2D object (typed FeaturePython)
  ChamferSize = 0
  Closed = true
  End = (-9.74768e+07,-6.32896e+07,34800)
  FilletRadius = 0
  Length = 37987.8
  MakeFace = true
  Points = (4) [(-97474900,-63297600,34800),(-97464300,-63299300,34800),(-97463500,-63294300,34800),(-97476800,-63289600,34800)]
  Start = (-9.74749e+07,-6.32976e+07,34800)
  Subdivisions = 0
FEATURE [Part::Extrusion] Extrusion001
  Base = -> DWire021
  Dir = (0,0,10950)
  Solid = true
FEATURE [Part::Extrusion] Extrusion002
  Base = -> DWire022
  Dir = (0,0,8800)
  Solid = true
FEATURE [Part::Extrusion] Extrude019
  Base = -> DWire023
  Dir = (0,0,3000)
  Solid = true
FEATURE [Part::Compound] Compound
  Links = -> [Extrude019,Extrusion002]
FEATURE [Part::Part2DObjectPython] DWire024  # Draft 2D object (typed FeaturePython)
  ChamferSize = 0
  Closed = true
  End = (-9.74715e+07,-6.33159e+07,0)
  FilletRadius = 0
  Length = 39302.5
  MakeFace = true
  Points = (5) [(-97467800,-63306300,0),(-97478400,-63305900,0),(-97479800,-63307600,0),(-97477300,-63317400,0),(-97471500,-63315900,0)]
  Start = (-9.74678e+07,-6.33063e+07,0)
  Subdivisions = 0
FEATURE [Part::Extrusion] Extrude020
  Base = -> DWire024
  Dir = (0,0,11000)
  Solid = true
FEATURE [Part::Part2DObjectPython] DWire025  # Draft 2D object (typed FeaturePython)
  ChamferSize = 0
  Closed = true
  End = (-9.74735e+07,-6.33316e+07,0)
  FilletRadius = 0
  Length = 41327.9
  MakeFace = true
  Points = (4) [(-97477300,-63317400,0),(-97471500,-63315900,0),(-97467700,-63330100,0),(-97473500,-63331600,0)]
  Start = (-9.74773e+07,-6.33174e+07,0)
  Subdivisions = 0
FEATURE [Part::Extrusion] Extrusion003
  Base = -> DWire025
  Dir = (0,0,10000)
  Solid = true
FEATURE [Part::Part2DObjectPython] DWire026  # Draft 2D object (typed FeaturePython)
  ChamferSize = 0
  Closed = true
  End = (-9.74677e+07,-6.33301e+07,26710)
  FilletRadius = 0
  Length = 33015.7
  MakeFace = true
  Points = (4) [(-97473500,-63331600,26710),(-97470800,-63341800,26710),(-97465000,-63340200,26710),(-97467700,-63330100,26710)]
  Start = (-9.74735e+07,-6.33316e+07,26710)
  Subdivisions = 0
FEATURE [Part::Extrusion] Extrusion004
  Base = -> DWire026
  Dir = (0,0,9680)
  Solid = true
FEATURE [Part::Part2DObjectPython] DWire028  label="DWire027"  # Draft 2D object (typed FeaturePython)
  ChamferSize = 0
  Closed = true
  End = (-9.7465e+07,-6.33402e+07,25000)
  FilletRadius = 0
  Length = 46015.1
  MakeFace = true
  Points = (4) [(-97470800,-63341800,25000),(-97464600,-63358000,25000),(-97459000,-63355800,25000),(-97465000,-63340200,25000)]
  Start = (-9.74708e+07,-6.33418e+07,25000)
  Subdivisions = 0
FEATURE [Part::Extrusion] Extrusion005
  Base = -> DWire028
  Dir = (0,0,9680)
  Solid = true
FEATURE [Part::Part2DObjectPython] DWire029  # Draft 2D object (typed FeaturePython)
  ChamferSize = 0
  Closed = true
  End = (-9.7459e+07,-6.33558e+07,26710)
  FilletRadius = 0
  Length = 33744.3
  MakeFace = true
  Points = (4) [(-97464600,-63358000,26710),(-97457200,-63367100,26710),(-97452500,-63363400,26710),(-97459000,-63355800,26710)]
  Start = (-9.74646e+07,-6.3358e+07,26710)
  Subdivisions = 0
FEATURE [Part::Extrusion] Extrusion006
  Base = -> DWire029
  Dir = (0,0,9680)
  Solid = true
FEATURE [Part::Part2DObjectPython] DWire030  label="25.75"  # Draft 2D object (typed FeaturePython)
  ChamferSize = 0
  Closed = true
  End = (-9.75358e+07,-6.33664e+07,0)
  FilletRadius = 0
  Length = 9292.31
  MakeFace = false
  Points = (6) [(-97536400,-63365700,0),(-97538900,-63365500,0),(-97539100,-63366600,0),(-97537500,-63368000,0),(-97536000,-63367400,0),(-97535800,-63366400,0)]
  Start = (-9.75364e+07,-6.33657e+07,0)
  Subdivisions = 0
FEATURE [Part::Part2DObjectPython] DWire031  label="25.5"  # Draft 2D object (typed FeaturePython)
  ChamferSize = 0
  Closed = true
  End = (-97520712,-63310748,25500)
  FilletRadius = 0
  Length = 6030.12
  MakeFace = false
  Points = (12) [(-97519900,-63310400,25500),(-97519600,-63310700,25500),(-97520000,-63310800,25500),(-97520400,-63311100,25500),(-97521100,-63311000,25500),+7 more]
  Start = (-9.75199e+07,-6.33104e+07,25500)
  Subdivisions = 0
FEATURE [Part::Part2DObjectPython] DWire032  label="25.076"  # Draft 2D object (typed FeaturePython)
  ChamferSize = 0
  Closed = true
  End = (-9.75441e+07,-6.33789e+07,0)
  FilletRadius = 0
  Length = 15989
  MakeFace = false
  Points = (9) [(-97542700,-63378600,0),(-97541800,-63377800,0),(-97540600,-63378500,0),(-97539800,-63379300,0),(-97539300,-63379500,0),(-97539300,-63379600,0),+3 more]
  Start = (-9.75427e+07,-6.33786e+07,0)
  Subdivisions = 0
FEATURE [Part::Part2DObjectPython] DWire033  label="25.077"  # Draft 2D object (typed FeaturePython)
  ChamferSize = 0
  Closed = true
  End = (-9.7539e+07,-6.33211e+07,0)
  FilletRadius = 0
  Length = 2396.37
  MakeFace = false
  Points = (4) [(-97538900,-63321700,0),(-97539800,-63321700,0),(-97539300,-63321100,0),(-97539000,-63321100,0)]
  Start = (-9.75389e+07,-6.33217e+07,0)
  Subdivisions = 0
FEATURE [Part::Part2DObjectPython] DWire034  label="25.078"  # Draft 2D object (typed FeaturePython)
  ChamferSize = 0
  Closed = true
  End = (-9.75264e+07,-6.33148e+07,0)
  FilletRadius = 0
  Length = 1510.71
  MakeFace = false
  Points = (3) [(-97527000,-63315100,0),(-97526500,-63315000,0),(-97526400,-63314800,0)]
  Start = (-9.7527e+07,-6.33151e+07,0)
  Subdivisions = 0
FEATURE [Part::Part2DObjectPython] DWire035  label="25.079"  # Draft 2D object (typed FeaturePython)
  ChamferSize = 0
  Closed = true
  End = (-9.75157e+07,-6.33084e+07,0)
  FilletRadius = 0
  Length = 5381.21
  MakeFace = false
  Points = (4) [(-97517100,-63309100,0),(-97516200,-63310000,0),(-97515500,-63310200,0),(-97515700,-63308400,0)]
  Start = (-9.75171e+07,-6.33091e+07,0)
  Subdivisions = 0
FEATURE [Part::Part2DObjectPython] DWire036  label="25.080"  # Draft 2D object (typed FeaturePython)
  ChamferSize = 0
  Closed = true
  End = (-97510608,-63305988,25750)
  FilletRadius = 0
  Length = 174553
  MakeFace = false
  Points = (71) [(-97509100,-63305100,25750),(-97508000,-63307600,25750),(-97507700,-63308000,25750),(-97510500,-63308200,25750),(-97511200,-63312200,25750),+66 more]
  Start = (-9.75091e+07,-6.33051e+07,25750)
  Subdivisions = 0
FEATURE [Part::Part2DObjectPython] DWire037  label="LIMITE"  # Draft 2D object (typed FeaturePython)
  ChamferSize = 0
  Closed = true
  End = (-9.75482e+07,-6.33327e+07,25000)
  FilletRadius = 0
  Length = 431357
  MakeFace = false
  Points = (49) [(-97554800,-63336300,25000),(-97558200,-63329200,25000),(-97550300,-63325600,25000),(-97539000,-63320500,25000),(-97523800,-63313700,25000),+44 more]
  Start = (-9.75548e+07,-6.33363e+07,25000)
  Subdivisions = 0
FEATURE [Part::Part2DObjectPython] DWire039  label="27.5"  # Draft 2D object (typed FeaturePython)
  ChamferSize = 0
  Closed = true
  End = (-9.74628e+07,-6.33654e+07,27500)
  FilletRadius = 0
  Length = 33256.2
  MakeFace = false
  Points = (9) [(-97468200,-63366300,27500),(-97468200,-63363500,27500),(-97468100,-63363200,27500),(-97467300,-63361300,27500),(-97466900,-63361300,27500),+4 more]
  Start = (-9.74682e+07,-6.33663e+07,27500)
  Subdivisions = 0
FEATURE [Part::Part2DObjectPython] DWire040  label="27.25"  # Draft 2D object (typed FeaturePython)
  ChamferSize = 0
  Closed = true
  End = (-97468304,-63368080,27250)
  FilletRadius = 0
  Length = 59349.9
  MakeFace = false
  Points = (15) [(-97475200,-63369300,27250),(-97475200,-63367900,27250),(-97474900,-63366400,27250),(-97474000,-63364200,27250),(-97469800,-63354300,27250),+10 more]
  Start = (-9.74752e+07,-6.33693e+07,27250)
  Subdivisions = 0
FEATURE [Part::Part2DObjectPython] DWire041  label="27"  # Draft 2D object (typed FeaturePython)
  ChamferSize = 0
  Closed = true
  End = (-9.74826e+07,-6.34004e+07,27000)
  FilletRadius = 0
  Length = 151957
  MakeFace = false
  Points = (26) [(-97482600,-63399200,27000),(-97482300,-63380200,27000),(-97482300,-63376800,27000),(-97482000,-63370800,27000),(-97481700,-63369600,27000),+21 more]
  Start = (-9.74826e+07,-6.33992e+07,27000)
  Subdivisions = 0
FEATURE [Part::Part2DObjectPython] DWire042  label="26.75"  # Draft 2D object (typed FeaturePython)
  ChamferSize = 0
  Closed = true
  End = (-9.74708e+07,-6.33418e+07,26750)
  FilletRadius = 0
  Length = 233656
  MakeFace = false
  Points = (56) [(-97472500,-63335400,26750),(-97473100,-63335700,26750),(-97474700,-63335800,26750),(-97473900,-63337300,26750),(-97474700,-63338400,26750),+51 more]
  Start = (-97472512,-63335368,26750)
  Subdivisions = 0
FEATURE [Part::Part2DObjectPython] DWire043  label="26.5"  # Draft 2D object (typed FeaturePython)
  ChamferSize = 0
  Closed = true
  End = (-97473952,-6.333e+07,26500)
  FilletRadius = 0
  Length = 258906
  MakeFace = false
  Points = (66) [(-97476800,-63319400,26500),(-97477700,-63319700,26500),(-97477800,-63320000,26500),(-97477700,-63321800,26500),(-97477500,-63321700,26500),+61 more]
  Start = (-97476752,-63319380,26500)
  Subdivisions = 0
FEATURE [Part::Part2DObjectPython] DWire044  label="26.25"  # Draft 2D object (typed FeaturePython)
  ChamferSize = 0
  Closed = true
  End = (-9.75074e+07,-6.33998e+07,26250)
  FilletRadius = 0
  Length = 342559
  MakeFace = false
  Points = (64) [(-97522900,-63398500,26250),(-97520200,-63395300,26250),(-97515100,-63393100,26250),(-97515800,-63389100,26250),(-97512800,-63380600,26250),+59 more]
  Start = (-97522904,-63398528,26250)
  Subdivisions = 0
FEATURE [Part::Part2DObjectPython] DWire045  label="26.076"  # Draft 2D object (typed FeaturePython)
  ChamferSize = 0
  Closed = true
  End = (-9.75443e+07,-6.3378e+07,26250)
  FilletRadius = 0
  Length = 3404.63
  MakeFace = false
  Points = (3) [(-97544700,-63378000,26250),(-97544500,-63379500,26250),(-97544300,-63378000,26250)]
  Start = (-9.75447e+07,-6.3378e+07,26250)
  Subdivisions = 0
FEATURE [Part::Part2DObjectPython] DWire046  label="26.077"  # Draft 2D object (typed FeaturePython)
  ChamferSize = 0
  Closed = true
  End = (-9.75346e+07,-6.33254e+07,26250)
  FilletRadius = 0
  Length = 709.541
  MakeFace = false
  Points = (3) [(-97534300,-63325200,26250),(-97534400,-63325200,26250),(-97534600,-63325400,26250)]
  Start = (-9.75343e+07,-6.33252e+07,26250)
  Subdivisions = 0
FEATURE [Part::Part2DObjectPython] DWire047  label="26"  # Draft 2D object (typed FeaturePython)
  ChamferSize = 0
  Closed = true
  End = (-9.75074e+07,-6.33998e+07,26000)
  FilletRadius = 0
  Length = 365101
  MakeFace = false
  Points = (94) [(-97539500,-63397100,26000),(-97539200,-63397000,26000),(-97530400,-63393100,26000),(-97530700,-63391700,26000),(-97527100,-63381500,26000),+89 more]
  Start = (-97539488,-63397136,26000)
  Subdivisions = 0
FEATURE [Part::Part2DObjectPython] DWire049  label="26001"  # Draft 2D object (typed FeaturePython)
  ChamferSize = 0
  Closed = true
  End = (-9.75475e+07,-6.33782e+07,26000)
  FilletRadius = 0
  Length = 26505.2
  MakeFace = false
  Points = (8) [(-97546000,-63388700,26000),(-97544100,-63378200,26000),(-97543400,-63378000,26000),(-97543400,-63377800,26000),(-97543700,-63377900,26000),+3 more]
  Start = (-9.7546e+07,-6.33887e+07,26000)
  Subdivisions = 0
FEATURE [Part::Part2DObjectPython] DWire050  label="26002"  # Draft 2D object (typed FeaturePython)
  ChamferSize = 0
  Closed = true
  End = (-97532096,-63325532,26000)
  FilletRadius = 0
  Length = 921.494
  MakeFace = false
  Points = (4) [(-97532100,-63325500,26000),(-97532400,-63325400,26000),(-97532200,-63325800,26000),(-97532100,-63325500,26000)]
  Start = (-9.75321e+07,-6.33255e+07,26000)
  Subdivisions = 0
FEATURE [Part::Part2DObjectPython] DWire051  label="26003"  # Draft 2D object (typed FeaturePython)
  ChamferSize = 0
  Closed = true
  End = (-9.75378e+07,-6.33271e+07,26000)
  FilletRadius = 0
  Length = 10949.8
  MakeFace = false
  Points = (4) [(-97533600,-63324900,26000),(-97535500,-63324200,26000),(-97538100,-63327100,26000),(-97537800,-63327100,26000)]
  Start = (-9.75336e+07,-6.33249e+07,26000)
  Subdivisions = 0
FEATURE [Part::Part2DObjectPython] DWire052  label="26004"  # Draft 2D object (typed FeaturePython)
  ChamferSize = 0
  Closed = true
  End = (-9.75516e+07,-6.33346e+07,26000)
  FilletRadius = 0
  Length = 74680
  MakeFace = false
  Points = (18) [(-97541000,-63328900,26000),(-97545800,-63329200,26000),(-97548900,-63328700,26000),(-97550700,-63328900,26000),(-97551100,-63326400,26000),+13 more]
  Start = (-9.7541e+07,-6.33289e+07,26000)
  Subdivisions = 0
FEATURE [Part::Part2DObjectPython] DWire053  label="26005"  # Draft 2D object (typed FeaturePython)
  ChamferSize = 0
  Closed = true
  End = (-9.75357e+07,-6.33465e+07,26000)
  FilletRadius = 0
  Length = 79800.8
  MakeFace = false
  Points = (15) [(-97541900,-63374300,26000),(-97540600,-63371900,26000),(-97538400,-63369600,26000),(-97540400,-63367900,26000),(-97539500,-63364400,26000),+10 more]
  Start = (-9.75419e+07,-6.33743e+07,26000)
  Subdivisions = 0
FEATURE [App::DocumentObjectGroup] Group004  label="curvas_nivel"
  Group = -> [DWire030,DWire031,DWire032,DWire033,DWire034,DWire035,DWire036,DWire039,DWire043,DWire040,DWire041,DWire042,DWire052,DWire053,DWire050,DWire049,DWire051,DWire046,DWire045,DWire047,DWire044,DWire037]
FEATURE [App::FeaturePython] Dimension  # Draft dimension (typed FeaturePython)
  Dimline = (-97527464,-63336800,26000)
  Direction = (0,0,0)
  Distance = 1671.84
  End = (-9.75266e+07,-6.33366e+07,26000)
  Normal = (0,0,1)
  Start = (-9.75282e+07,-6.33363e+07,26000)
FEATURE [Part::Part2DObjectPython] Line004  # Draft 2D object (typed FeaturePython)
  ChamferSize = 0
  Closed = false
  End = (-9.75363e+07,-6.33734e+07,26000)
  FilletRadius = 0
  Length = 3835.25
  MakeFace = true
  Points = (2) [(-97535500,-63369700,26000),(-97536300,-63373400,26000)]
  Start = (-9.75355e+07,-6.33697e+07,26000)
  Subdivisions = 0
FEATURE [Part::Part2DObjectPython] Line005  # Draft 2D object (typed FeaturePython)
  ChamferSize = 0
  Closed = false
  End = (-9.75343e+07,-6.33738e+07,26000)
  FilletRadius = 0
  Length = 3835.25
  MakeFace = true
  Points = (2) [(-97533500,-63370100,26000),(-97534300,-63373800,26000)]
  Start = (-9.75335e+07,-6.33701e+07,26000)
  Subdivisions = 0
FEATURE [Part::Part2DObjectPython] Rectangle001  # Draft 2D object (typed FeaturePython)
  ChamferSize = 0
  Columns = 1
  FilletRadius = 0
  Height = 8000
  Length = 40000
  MakeFace = true
  Placement = pos=(-9.75257e+07,-6.33718e+07,26000) rot=(0,0,1;1.35374rad)
  Rows = 1
FEATURE [Part::Extrusion] Extrude021
  Base = -> Rectangle001
  Dir = (0,0,10000)
  Solid = true
FEATURE [Part::Part2DObjectPython] DWire054  # Draft 2D object (typed FeaturePython)
  ChamferSize = 0
  Closed = true
  End = (-9.75201e+07,-6.33464e+07,26000)
  FilletRadius = 0
  Length = 112683
  MakeFace = true
  Points = (8) [(-97525700,-63371800,26000),(-97495200,-63371800,26000),(-97489800,-63371400,26000),(-97489600,-63366600,26000),(-97491000,-63366600,26000),+3 more]
  Start = (-9.75257e+07,-6.33718e+07,26000)
  Subdivisions = 0
FEATURE [Part::Extrusion] Extrude022
  Base = -> DWire054
  Dir = (0,0,7000)
  Solid = true
FEATURE [Part::Part2DObjectPython] Rectangle002  # Draft 2D object (typed FeaturePython)
  ChamferSize = 0
  Columns = 1
  FilletRadius = 0
  Height = 12237.7
  Length = 25081.9
  MakeFace = true
  Placement = pos=(-97491256,-63324944,26000) rot=(0,0,-1;1.32599rad)
  Rows = 1
FEATURE [Part::Extrusion] Extrude023
  Base = -> Rectangle002
  Dir = (0,0,9000)
  Solid = true
FEATURE [Part::Part2DObjectPython] Rectangle  # Draft 2D object (typed FeaturePython)
  ChamferSize = 0
  Columns = 1
  FilletRadius = 0
  Height = 7000
  Length = -40000
  MakeFace = true
  Placement = pos=(-97473304,-63346312,26000) rot=(0,0,1;0.259343rad)
  Rows = 1
FEATURE [Part::Extrusion] Extrude024
  Base = -> Rectangle
  Dir = (0,0,12000)
  Solid = true
FEATURE [Part::Part2DObjectPython] Rectangle005  # Draft 2D object (typed FeaturePython)
  ChamferSize = 0
  Columns = 1
  FilletRadius = 0
  Height = 4000
  Length = -16000
  MakeFace = true
  Placement = pos=(-9.75057e+07,-6.33313e+07,26000) rot=(0,0,1;3.3438rad)
  Rows = 1
FEATURE [Part::Part2DObjectPython] Rectangle006  # Draft 2D object (typed FeaturePython)
  ChamferSize = 0
  Columns = 1
  FilletRadius = 0
  Height = 4000
  Length = 20000
  MakeFace = true
  Placement = pos=(-9.75017e+07,-6.33305e+07,26000) rot=(0,0,1;1.80398rad)
  Rows = 1
FEATURE [Part::Extrusion] Extrude025
  Base = -> Rectangle006
  Dir = (0,0,5000)
  Solid = true
FEATURE [Part::Extrusion] Extrude026
  Base = -> Rectangle005
  Dir = (0,0,5000)
  Solid = true
FEATURE [Part::Part2DObjectPython] DWire056  # Draft 2D object (typed FeaturePython)
  ChamferSize = 0
  Closed = true
  End = (-9.74968e+07,-6.3323e+07,26000)
  FilletRadius = 0
  Length = 45292.2
  MakeFace = true
  Points = (5) [(-97503200,-63324200,26000),(-97506400,-63311000,26000),(-97506600,-63310200,26000),(-97499600,-63306700,26000),(-97496800,-63323000,26000)]
  Start = (-97503250,-63324150,26000)
  Subdivisions = 0
FEATURE [Part::Extrusion] Extrude027
  Base = -> DWire056
  Dir = (0,0,7000)
  Solid = true
FEATURE [Part::Part2DObjectPython] DWire057  # Draft 2D object (typed FeaturePython)
  ChamferSize = 0
  Closed = true
  End = (-9.75009e+07,-6.33784e+07,26000)
  FilletRadius = 0
  Length = 123852
  MakeFace = true
  Points = (8) [(-97501100,-63373600,26000),(-97518800,-63326900,26000),(-97515100,-63325400,26000),(-97494800,-63352000,26000),(-97495900,-63365700,26000),+3 more]
  Start = (-9.75011e+07,-6.33736e+07,26000)
  Subdivisions = 0
FEATURE [Part::Extrusion] Extrude028
  Base = -> DWire057
  Dir = (0,0,4000)
  Solid = true
FEATURE [Part::Cut] Cut
  Base = -> Extrude022
  Tool = -> Extrude028
FEATURE [Part::FeaturePython] Clone001  label="Clone of Extrude028"  # Draft clone (typed FeaturePython)
  Objects = -> [Extrude028]
  Scale = (1,1,1)
FEATURE [Part::Cut] Cut001
  Base = -> Extrude024
  Tool = -> Clone001
FEATURE [App::DocumentObjectGroup] Group005  label="volumes_proposta"
  Group = -> [Extrude021,Extrude023,Extrude025,Extrude026,Extrude027,Cut,Cut001]
FEATURE [Part::Part2DObjectPython] DWire058  # Draft 2D object (typed FeaturePython)
  ChamferSize = 0
  Closed = true
  End = (-97511904,-63375524,37810)
  FilletRadius = 0
  Length = 84508.6
  MakeFace = false
  Points = (4) [(-97537600,-63377700,37810),(-97538300,-63393200,37810),(-97511300,-63391700,37810),(-97511900,-63375500,37810)]
  Start = (-9.75376e+07,-6.33777e+07,37810)
  Subdivisions = 0
FEATURE [Part::FeaturePython] Roof  # WARN: FeaturePython — macro-defined, semantics opaque (R4)
  Angles = [90,30,90,30]
  Base = -> DWire058
  Face = 0
  Heights = [0,4907.48,0,4907.48]
  IdRel = [0,0,0,0]
  MoveWithHost = false
  Overhang = [-700,250,100,250]
  Role = 0
  Runs = [8500,8500,8500,8500]
  Thickness = [100,100,100,100]
FEATURE [Part::FeaturePython] Wall  # WARN: FeaturePython — macro-defined, semantics opaque (R4)
  Align = 2
  Base = -> Extrude009
  Face = 0
  Height = 3000
  Length = 0
  MoveWithHost = false
  Normal = (0,0,0)
  Role = 0
  Subtractions = -> [Roof]
  Width = 200
FEATURE [Part::Part2DObjectPython] DWire059  # Draft 2D object (typed FeaturePython)
  ChamferSize = 0
  Closed = true
  End = (-97538296,-63393164,37810)
  FilletRadius = 0
  Length = 19928.2
  MakeFace = false
  Points = (4) [(-97538100,-63388000,37810),(-97533300,-63388000,37810),(-97533300,-63392900,37810),(-97538300,-63393200,37810)]
  Start = (-9.75381e+07,-6.3388e+07,37810)
  Subdivisions = 0
FEATURE [Part::Extrusion] Extrusion007
  Base = -> DWire059
  Dir = (0,0,9000)
  Solid = true
FEATURE [Part::MultiFuse] Fusion
  Shapes = -> [Extrusion007,Wall]
FEATURE [App::DocumentObjectGroupPython] Building  # scripted group (container) (typed FeaturePython)
  BuildingType = 80
  Group = -> [Fusion]
  Height = 0
FEATURE [App::DocumentObjectGroup] Group003  label="volumes"
  Group = -> [Extrusion006,Extrude007,Extrude,Extrude001,DWire001,Extrude002,Line,DWire002,Extrude003,DWire003,Extrude004,Extrude005,Extrude006,Extrude008,DWire009,Extrude009,Line001,Line003,Compound,Extrude010,Extrusion005,Extrusion004,Extrusion003,Extrude020,Extrusion001,Extrusion,DWire019,Extrude018,DWire020,Extrude017,Extrude016,Extrude015,DWire014,Extrude012,Extrude013,DWire021,Extrude014,Extrude011,Roof,+2 more]
FEATURE [App::FeaturePython] Section  label="Section1"  # WARN: FeaturePython — macro-defined, semantics opaque (R4)
  Objects = -> [Extrude028,Group005,Group003]
  OnlySolids = true
  Placement = pos=(-9.75097e+07,-6.33499e+07,28000) rot=(0.71527,-0.49416,-0.49416;1.89979rad)
FEATURE [App::FeaturePython] Section001  label="Section2"  # WARN: FeaturePython — macro-defined, semantics opaque (R4)
  Objects = -> [Cut,Group005,Group003]
  OnlySolids = true
  Placement = pos=(-9.75059e+07,-6.33598e+07,28000) rot=(0.438943,0.635346,0.635346;2.31435rad)
FEATURE [App::FeaturePython] Section002  label="Section"  # WARN: FeaturePython — macro-defined, semantics opaque (R4)
  Objects = -> [Cut001]
  OnlySolids = true
  Placement = pos=(-97491500,-63200000,32512.4) rot=(0.983417,0.128241,0.128241;1.58752rad)
FEATURE [Part::FeaturePython] Clone  label="Clone of Cut"  # Draft clone (typed FeaturePython)
  Objects = -> [Cut]
  Scale = (1,1,1)
FEATURE [Part::FeaturePython] Clone002  label="Clone of Extrude021"  # Draft clone (typed FeaturePython)
  Objects = -> [Extrude021]
  Scale = (1,1,1)
FEATURE [Part::FeaturePython] Space  # WARN: FeaturePython — macro-defined, semantics opaque (R4)
  Area = 4.04418e+08
  Base = -> Clone
  FloorThickness = 0
  MoveWithHost = false
  Role = 0
  SpaceType = -1
FEATURE [Part::FeaturePython] Space001  label="Space"  # WARN: FeaturePython — macro-defined, semantics opaque (R4)
  Area = 3.2e+08
  Base = -> Clone002
  FloorThickness = 0
  MoveWithHost = false
  Role = 0
  SpaceType = -1
FEATURE [App::DocumentObjectGroup] Grupo  label="areas"
  Group = -> [Space001,Space]
